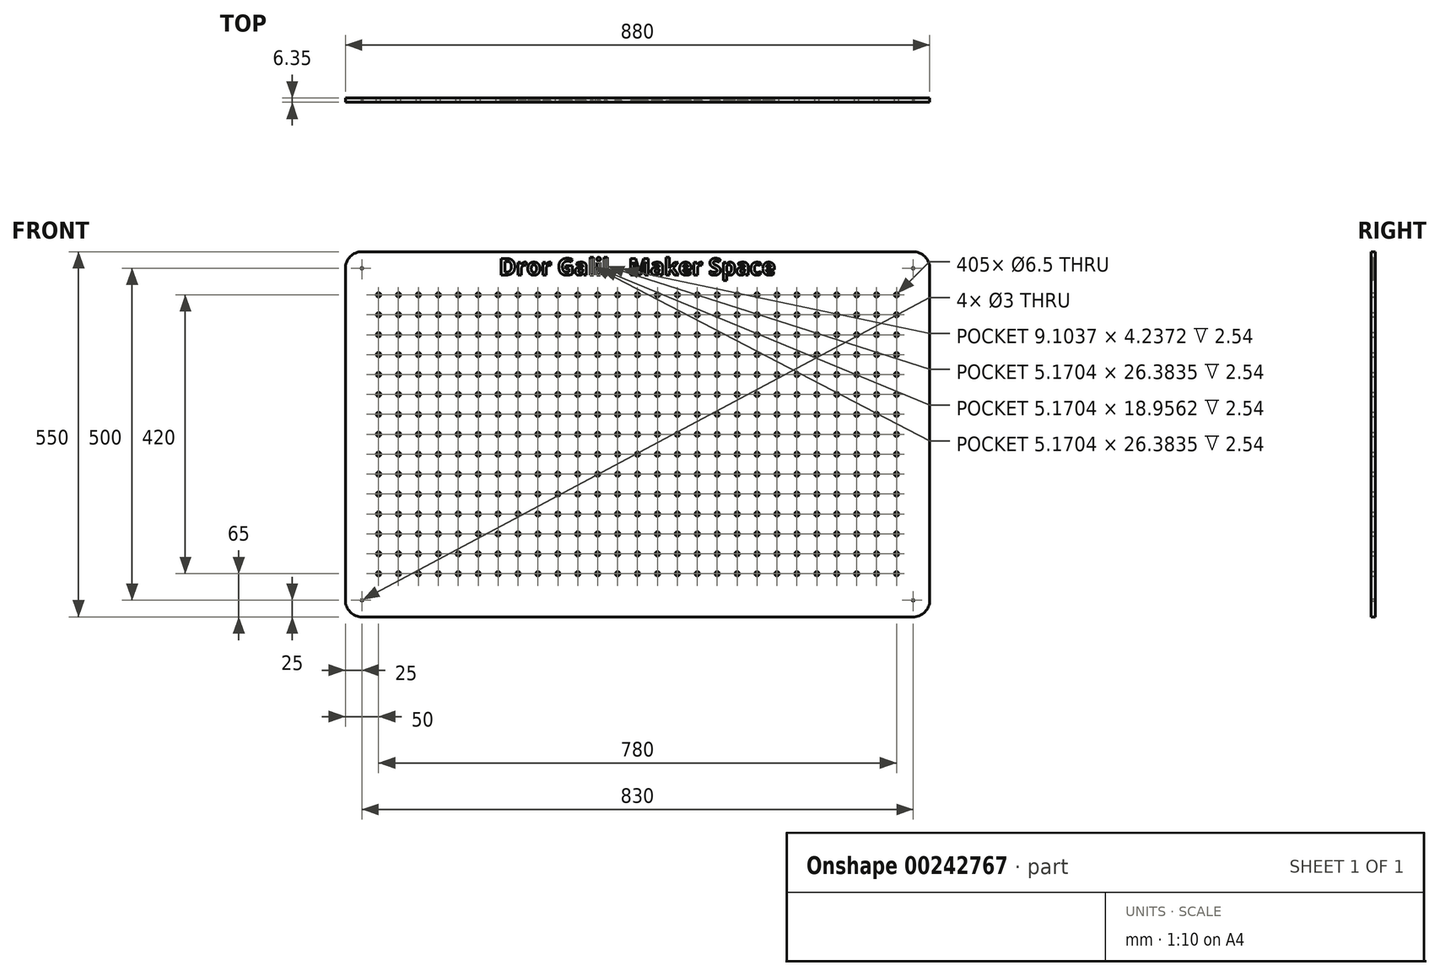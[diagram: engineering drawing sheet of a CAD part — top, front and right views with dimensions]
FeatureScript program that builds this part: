
annotation { "Feature Type Name" : "Feature", "Feature Type Description" : "" }
export const myFeature = defineFeature(function(context is Context, id is Id, definition is map)
    precondition{}
    {
        {
            var Q0;
            Q0=qCreatedBy(makeId("Front.planeOp"),FACE);
            var sketch = newSketch(context, id + "F0", { "sketchPlane" : qUnion([Q0])});
            skLineSegment(sketch, "E0.bottom", {"start": v(-440, 275) * mm, "end": v(440, 275) * mm});
            skLineSegment(sketch, "E0.top", {"start": v(-440, -275) * mm, "end": v(440, -275) * mm});
            skLineSegment(sketch, "E0.left", {"start": v(-440, 275) * mm, "end": v(-440, -275) * mm});
            skLineSegment(sketch, "E1", {"start": v(-390, 275) * mm, "end": v(-390, 210) * mm, "construction": true});
            skLineSegment(sketch, "E2", {"start": v(-390, 210) * mm, "end": v(-440, 210) * mm, "construction": true});
            skCircle(sketch, "E3", {"center": v(-390, 210) * mm, "radius": 3.25 * mm});
            skLineSegment(sketch, "E4", {"start": v(440, 275) * mm, "end": v(440, -275) * mm});
            skLineSegment(sketch, "E5", {"start": v(-48.1, 0) * mm, "end": v(43.52, 0) * mm, "construction": true});
            skLineSegment(sketch, "E6", {"start": v(0, 55.66) * mm, "end": v(0, -47.1) * mm, "construction": true});
            skCircle(sketch, "E7.0.1.0", {"center": v(-390, 180) * mm, "radius": 3.25 * mm});
            skCircle(sketch, "E7.0.2.0", {"center": v(-390, 150) * mm, "radius": 3.25 * mm});
            skCircle(sketch, "E7.0.3.0", {"center": v(-390, 120) * mm, "radius": 3.25 * mm});
            skCircle(sketch, "E7.0.4.0", {"center": v(-390, 90) * mm, "radius": 3.25 * mm});
            skCircle(sketch, "E7.0.5.0", {"center": v(-390, 60) * mm, "radius": 3.25 * mm});
            skCircle(sketch, "E7.0.6.0", {"center": v(-390, 30) * mm, "radius": 3.25 * mm});
            skCircle(sketch, "E7.0.7.0", {"center": v(-390, 0) * mm, "radius": 3.25 * mm});
            skCircle(sketch, "E7.0.8.0", {"center": v(-390, -30) * mm, "radius": 3.25 * mm});
            skCircle(sketch, "E7.1.0.0", {"center": v(-360, 210) * mm, "radius": 3.25 * mm});
            skCircle(sketch, "E7.1.1.0", {"center": v(-360, 180) * mm, "radius": 3.25 * mm});
            skCircle(sketch, "E7.1.2.0", {"center": v(-360, 150) * mm, "radius": 3.25 * mm});
            skCircle(sketch, "E7.1.3.0", {"center": v(-360, 120) * mm, "radius": 3.25 * mm});
            skCircle(sketch, "E7.1.4.0", {"center": v(-360, 90) * mm, "radius": 3.25 * mm});
            skCircle(sketch, "E7.1.5.0", {"center": v(-360, 60) * mm, "radius": 3.25 * mm});
            skCircle(sketch, "E7.1.6.0", {"center": v(-360, 30) * mm, "radius": 3.25 * mm});
            skCircle(sketch, "E7.1.7.0", {"center": v(-360, 0) * mm, "radius": 3.25 * mm});
            skCircle(sketch, "E7.1.8.0", {"center": v(-360, -30) * mm, "radius": 3.25 * mm});
            skCircle(sketch, "E7.2.0.0", {"center": v(-330, 210) * mm, "radius": 3.25 * mm});
            skCircle(sketch, "E7.2.1.0", {"center": v(-330, 180) * mm, "radius": 3.25 * mm});
            skCircle(sketch, "E7.2.2.0", {"center": v(-330, 150) * mm, "radius": 3.25 * mm});
            skCircle(sketch, "E7.2.3.0", {"center": v(-330, 120) * mm, "radius": 3.25 * mm});
            skCircle(sketch, "E7.2.4.0", {"center": v(-330, 90) * mm, "radius": 3.25 * mm});
            skCircle(sketch, "E7.2.5.0", {"center": v(-330, 60) * mm, "radius": 3.25 * mm});
            skCircle(sketch, "E7.2.6.0", {"center": v(-330, 30) * mm, "radius": 3.25 * mm});
            skCircle(sketch, "E7.2.7.0", {"center": v(-330, 0) * mm, "radius": 3.25 * mm});
            skCircle(sketch, "E7.2.8.0", {"center": v(-330, -30) * mm, "radius": 3.25 * mm});
            skCircle(sketch, "E7.3.0.0", {"center": v(-300, 210) * mm, "radius": 3.25 * mm});
            skCircle(sketch, "E7.3.1.0", {"center": v(-300, 180) * mm, "radius": 3.25 * mm});
            skCircle(sketch, "E7.3.2.0", {"center": v(-300, 150) * mm, "radius": 3.25 * mm});
            skCircle(sketch, "E7.3.3.0", {"center": v(-300, 120) * mm, "radius": 3.25 * mm});
            skCircle(sketch, "E7.3.4.0", {"center": v(-300, 90) * mm, "radius": 3.25 * mm});
            skCircle(sketch, "E7.3.5.0", {"center": v(-300, 60) * mm, "radius": 3.25 * mm});
            skCircle(sketch, "E7.3.6.0", {"center": v(-300, 30) * mm, "radius": 3.25 * mm});
            skCircle(sketch, "E7.3.7.0", {"center": v(-300, 0) * mm, "radius": 3.25 * mm});
            skCircle(sketch, "E7.3.8.0", {"center": v(-300, -30) * mm, "radius": 3.25 * mm});
            skCircle(sketch, "E7.4.0.0", {"center": v(-270, 210) * mm, "radius": 3.25 * mm});
            skCircle(sketch, "E7.4.1.0", {"center": v(-270, 180) * mm, "radius": 3.25 * mm});
            skCircle(sketch, "E7.4.2.0", {"center": v(-270, 150) * mm, "radius": 3.25 * mm});
            skCircle(sketch, "E7.4.3.0", {"center": v(-270, 120) * mm, "radius": 3.25 * mm});
            skCircle(sketch, "E7.4.4.0", {"center": v(-270, 90) * mm, "radius": 3.25 * mm});
            skCircle(sketch, "E7.4.5.0", {"center": v(-270, 60) * mm, "radius": 3.25 * mm});
            skCircle(sketch, "E7.4.6.0", {"center": v(-270, 30) * mm, "radius": 3.25 * mm});
            skCircle(sketch, "E7.4.7.0", {"center": v(-270, 0) * mm, "radius": 3.25 * mm});
            skCircle(sketch, "E7.4.8.0", {"center": v(-270, -30) * mm, "radius": 3.25 * mm});
            skCircle(sketch, "E7.5.0.0", {"center": v(-240, 210) * mm, "radius": 3.25 * mm});
            skCircle(sketch, "E7.5.1.0", {"center": v(-240, 180) * mm, "radius": 3.25 * mm});
            skCircle(sketch, "E7.5.2.0", {"center": v(-240, 150) * mm, "radius": 3.25 * mm});
            skCircle(sketch, "E7.5.3.0", {"center": v(-240, 120) * mm, "radius": 3.25 * mm});
            skCircle(sketch, "E7.5.4.0", {"center": v(-240, 90) * mm, "radius": 3.25 * mm});
            skCircle(sketch, "E7.5.5.0", {"center": v(-240, 60) * mm, "radius": 3.25 * mm});
            skCircle(sketch, "E7.5.6.0", {"center": v(-240, 30) * mm, "radius": 3.25 * mm});
            skCircle(sketch, "E7.5.7.0", {"center": v(-240, 0) * mm, "radius": 3.25 * mm});
            skCircle(sketch, "E7.5.8.0", {"center": v(-240, -30) * mm, "radius": 3.25 * mm});
            skCircle(sketch, "E7.6.0.0", {"center": v(-210, 210) * mm, "radius": 3.25 * mm});
            skCircle(sketch, "E7.6.1.0", {"center": v(-210, 180) * mm, "radius": 3.25 * mm});
            skCircle(sketch, "E7.6.2.0", {"center": v(-210, 150) * mm, "radius": 3.25 * mm});
            skCircle(sketch, "E7.6.3.0", {"center": v(-210, 120) * mm, "radius": 3.25 * mm});
            skCircle(sketch, "E7.6.4.0", {"center": v(-210, 90) * mm, "radius": 3.25 * mm});
            skCircle(sketch, "E7.6.5.0", {"center": v(-210, 60) * mm, "radius": 3.25 * mm});
            skCircle(sketch, "E7.6.6.0", {"center": v(-210, 30) * mm, "radius": 3.25 * mm});
            skCircle(sketch, "E7.6.7.0", {"center": v(-210, 0) * mm, "radius": 3.25 * mm});
            skCircle(sketch, "E7.6.8.0", {"center": v(-210, -30) * mm, "radius": 3.25 * mm});
            skCircle(sketch, "E7.7.0.0", {"center": v(-180, 210) * mm, "radius": 3.25 * mm});
            skCircle(sketch, "E7.7.1.0", {"center": v(-180, 180) * mm, "radius": 3.25 * mm});
            skCircle(sketch, "E7.7.2.0", {"center": v(-180, 150) * mm, "radius": 3.25 * mm});
            skCircle(sketch, "E7.7.3.0", {"center": v(-180, 120) * mm, "radius": 3.25 * mm});
            skCircle(sketch, "E7.7.4.0", {"center": v(-180, 90) * mm, "radius": 3.25 * mm});
            skCircle(sketch, "E7.7.5.0", {"center": v(-180, 60) * mm, "radius": 3.25 * mm});
            skCircle(sketch, "E7.7.6.0", {"center": v(-180, 30) * mm, "radius": 3.25 * mm});
            skCircle(sketch, "E7.7.7.0", {"center": v(-180, 0) * mm, "radius": 3.25 * mm});
            skCircle(sketch, "E7.7.8.0", {"center": v(-180, -30) * mm, "radius": 3.25 * mm});
            skCircle(sketch, "E7.8.0.0", {"center": v(-150, 210) * mm, "radius": 3.25 * mm});
            skCircle(sketch, "E7.8.1.0", {"center": v(-150, 180) * mm, "radius": 3.25 * mm});
            skCircle(sketch, "E7.8.2.0", {"center": v(-150, 150) * mm, "radius": 3.25 * mm});
            skCircle(sketch, "E7.8.3.0", {"center": v(-150, 120) * mm, "radius": 3.25 * mm});
            skCircle(sketch, "E7.8.4.0", {"center": v(-150, 90) * mm, "radius": 3.25 * mm});
            skCircle(sketch, "E7.8.5.0", {"center": v(-150, 60) * mm, "radius": 3.25 * mm});
            skCircle(sketch, "E7.8.6.0", {"center": v(-150, 30) * mm, "radius": 3.25 * mm});
            skCircle(sketch, "E7.8.7.0", {"center": v(-150, 0) * mm, "radius": 3.25 * mm});
            skCircle(sketch, "E7.8.8.0", {"center": v(-150, -30) * mm, "radius": 3.25 * mm});
            skCircle(sketch, "E7.9.0.0", {"center": v(-120, 210) * mm, "radius": 3.25 * mm});
            skCircle(sketch, "E7.9.1.0", {"center": v(-120, 180) * mm, "radius": 3.25 * mm});
            skCircle(sketch, "E7.9.2.0", {"center": v(-120, 150) * mm, "radius": 3.25 * mm});
            skCircle(sketch, "E7.9.3.0", {"center": v(-120, 120) * mm, "radius": 3.25 * mm});
            skCircle(sketch, "E7.9.4.0", {"center": v(-120, 90) * mm, "radius": 3.25 * mm});
            skCircle(sketch, "E7.9.5.0", {"center": v(-120, 60) * mm, "radius": 3.25 * mm});
            skCircle(sketch, "E7.9.6.0", {"center": v(-120, 30) * mm, "radius": 3.25 * mm});
            skCircle(sketch, "E7.9.7.0", {"center": v(-120, 0) * mm, "radius": 3.25 * mm});
            skCircle(sketch, "E7.9.8.0", {"center": v(-120, -30) * mm, "radius": 3.25 * mm});
            skCircle(sketch, "E7.10.0.0", {"center": v(-90, 210) * mm, "radius": 3.25 * mm});
            skCircle(sketch, "E7.10.1.0", {"center": v(-90, 180) * mm, "radius": 3.25 * mm});
            skCircle(sketch, "E7.10.2.0", {"center": v(-90, 150) * mm, "radius": 3.25 * mm});
            skCircle(sketch, "E7.10.3.0", {"center": v(-90, 120) * mm, "radius": 3.25 * mm});
            skCircle(sketch, "E7.10.4.0", {"center": v(-90, 90) * mm, "radius": 3.25 * mm});
            skCircle(sketch, "E7.10.5.0", {"center": v(-90, 60) * mm, "radius": 3.25 * mm});
            skCircle(sketch, "E7.10.6.0", {"center": v(-90, 30) * mm, "radius": 3.25 * mm});
            skCircle(sketch, "E7.10.7.0", {"center": v(-90, 0) * mm, "radius": 3.25 * mm});
            skCircle(sketch, "E7.10.8.0", {"center": v(-90, -30) * mm, "radius": 3.25 * mm});
            skCircle(sketch, "E7.11.0.0", {"center": v(-60, 210) * mm, "radius": 3.25 * mm});
            skCircle(sketch, "E7.11.1.0", {"center": v(-60, 180) * mm, "radius": 3.25 * mm});
            skCircle(sketch, "E7.11.2.0", {"center": v(-60, 150) * mm, "radius": 3.25 * mm});
            skCircle(sketch, "E7.11.3.0", {"center": v(-60, 120) * mm, "radius": 3.25 * mm});
            skCircle(sketch, "E7.11.4.0", {"center": v(-60, 90) * mm, "radius": 3.25 * mm});
            skCircle(sketch, "E7.11.5.0", {"center": v(-60, 60) * mm, "radius": 3.25 * mm});
            skCircle(sketch, "E7.11.6.0", {"center": v(-60, 30) * mm, "radius": 3.25 * mm});
            skCircle(sketch, "E7.11.7.0", {"center": v(-60, 0) * mm, "radius": 3.25 * mm});
            skCircle(sketch, "E7.11.8.0", {"center": v(-60, -30) * mm, "radius": 3.25 * mm});
            skCircle(sketch, "E7.12.0.0", {"center": v(-30, 210) * mm, "radius": 3.25 * mm});
            skCircle(sketch, "E7.12.1.0", {"center": v(-30, 180) * mm, "radius": 3.25 * mm});
            skCircle(sketch, "E7.12.2.0", {"center": v(-30, 150) * mm, "radius": 3.25 * mm});
            skCircle(sketch, "E7.12.3.0", {"center": v(-30, 120) * mm, "radius": 3.25 * mm});
            skCircle(sketch, "E7.12.4.0", {"center": v(-30, 90) * mm, "radius": 3.25 * mm});
            skCircle(sketch, "E7.12.5.0", {"center": v(-30, 60) * mm, "radius": 3.25 * mm});
            skCircle(sketch, "E7.12.6.0", {"center": v(-30, 30) * mm, "radius": 3.25 * mm});
            skCircle(sketch, "E7.12.7.0", {"center": v(-30, 0) * mm, "radius": 3.25 * mm});
            skCircle(sketch, "E7.12.8.0", {"center": v(-30, -30) * mm, "radius": 3.25 * mm});
            skCircle(sketch, "E7.13.0.0", {"center": v(0, 210) * mm, "radius": 3.25 * mm});
            skCircle(sketch, "E7.13.1.0", {"center": v(0, 180) * mm, "radius": 3.25 * mm});
            skCircle(sketch, "E7.13.2.0", {"center": v(0, 150) * mm, "radius": 3.25 * mm});
            skCircle(sketch, "E7.13.3.0", {"center": v(0, 120) * mm, "radius": 3.25 * mm});
            skCircle(sketch, "E7.13.4.0", {"center": v(0, 90) * mm, "radius": 3.25 * mm});
            skCircle(sketch, "E7.13.5.0", {"center": v(0, 60) * mm, "radius": 3.25 * mm});
            skCircle(sketch, "E7.13.6.0", {"center": v(0, 30) * mm, "radius": 3.25 * mm});
            skCircle(sketch, "E7.13.7.0", {"center": v(0, 0) * mm, "radius": 3.25 * mm});
            skCircle(sketch, "E7.13.8.0", {"center": v(0, -30) * mm, "radius": 3.25 * mm});
            skCircle(sketch, "E7.14.0.0", {"center": v(30, 210) * mm, "radius": 3.25 * mm});
            skCircle(sketch, "E7.14.1.0", {"center": v(30, 180) * mm, "radius": 3.25 * mm});
            skCircle(sketch, "E7.14.2.0", {"center": v(30, 150) * mm, "radius": 3.25 * mm});
            skCircle(sketch, "E7.14.3.0", {"center": v(30, 120) * mm, "radius": 3.25 * mm});
            skCircle(sketch, "E7.14.4.0", {"center": v(30, 90) * mm, "radius": 3.25 * mm});
            skCircle(sketch, "E7.14.5.0", {"center": v(30, 60) * mm, "radius": 3.25 * mm});
            skCircle(sketch, "E7.14.6.0", {"center": v(30, 30) * mm, "radius": 3.25 * mm});
            skCircle(sketch, "E7.14.7.0", {"center": v(30, 0) * mm, "radius": 3.25 * mm});
            skCircle(sketch, "E7.14.8.0", {"center": v(30, -30) * mm, "radius": 3.25 * mm});
            skLineSegment(sketch, "E7.direction1", {"start": v(-390, 210) * mm, "end": v(-360, 210) * mm, "construction": true});
            skLineSegment(sketch, "E7.direction2", {"start": v(-390, 210) * mm, "end": v(-390, 180) * mm, "construction": true});
            skCircle(sketch, "E8.0.15.0", {"center": v(60, 210) * mm, "radius": 3.25 * mm});
            skCircle(sketch, "E8.0.15.1", {"center": v(60, 180) * mm, "radius": 3.25 * mm});
            skCircle(sketch, "E8.0.15.2", {"center": v(60, 150) * mm, "radius": 3.25 * mm});
            skCircle(sketch, "E8.0.15.3", {"center": v(60, 120) * mm, "radius": 3.25 * mm});
            skCircle(sketch, "E8.0.15.4", {"center": v(60, 90) * mm, "radius": 3.25 * mm});
            skCircle(sketch, "E8.0.15.5", {"center": v(60, 60) * mm, "radius": 3.25 * mm});
            skCircle(sketch, "E8.0.15.6", {"center": v(60, 30) * mm, "radius": 3.25 * mm});
            skCircle(sketch, "E8.0.15.7", {"center": v(60, 0) * mm, "radius": 3.25 * mm});
            skCircle(sketch, "E8.0.15.8", {"center": v(60, -30) * mm, "radius": 3.25 * mm});
            skCircle(sketch, "E8.0.16.0", {"center": v(90, 210) * mm, "radius": 3.25 * mm});
            skCircle(sketch, "E8.0.16.1", {"center": v(90, 180) * mm, "radius": 3.25 * mm});
            skCircle(sketch, "E8.0.16.2", {"center": v(90, 150) * mm, "radius": 3.25 * mm});
            skCircle(sketch, "E8.0.16.3", {"center": v(90, 120) * mm, "radius": 3.25 * mm});
            skCircle(sketch, "E8.0.16.4", {"center": v(90, 90) * mm, "radius": 3.25 * mm});
            skCircle(sketch, "E8.0.16.5", {"center": v(90, 60) * mm, "radius": 3.25 * mm});
            skCircle(sketch, "E8.0.16.6", {"center": v(90, 30) * mm, "radius": 3.25 * mm});
            skCircle(sketch, "E8.0.16.7", {"center": v(90, 0) * mm, "radius": 3.25 * mm});
            skCircle(sketch, "E8.0.16.8", {"center": v(90, -30) * mm, "radius": 3.25 * mm});
            skCircle(sketch, "E8.0.17.0", {"center": v(120, 210) * mm, "radius": 3.25 * mm});
            skCircle(sketch, "E8.0.17.1", {"center": v(120, 180) * mm, "radius": 3.25 * mm});
            skCircle(sketch, "E8.0.17.2", {"center": v(120, 150) * mm, "radius": 3.25 * mm});
            skCircle(sketch, "E8.0.17.3", {"center": v(120, 120) * mm, "radius": 3.25 * mm});
            skCircle(sketch, "E8.0.17.4", {"center": v(120, 90) * mm, "radius": 3.25 * mm});
            skCircle(sketch, "E8.0.17.5", {"center": v(120, 60) * mm, "radius": 3.25 * mm});
            skCircle(sketch, "E8.0.17.6", {"center": v(120, 30) * mm, "radius": 3.25 * mm});
            skCircle(sketch, "E8.0.17.7", {"center": v(120, 0) * mm, "radius": 3.25 * mm});
            skCircle(sketch, "E8.0.17.8", {"center": v(120, -30) * mm, "radius": 3.25 * mm});
            skCircle(sketch, "E8.0.18.0", {"center": v(150, 210) * mm, "radius": 3.25 * mm});
            skCircle(sketch, "E8.0.18.1", {"center": v(150, 180) * mm, "radius": 3.25 * mm});
            skCircle(sketch, "E8.0.18.2", {"center": v(150, 150) * mm, "radius": 3.25 * mm});
            skCircle(sketch, "E8.0.18.3", {"center": v(150, 120) * mm, "radius": 3.25 * mm});
            skCircle(sketch, "E8.0.18.4", {"center": v(150, 90) * mm, "radius": 3.25 * mm});
            skCircle(sketch, "E8.0.18.5", {"center": v(150, 60) * mm, "radius": 3.25 * mm});
            skCircle(sketch, "E8.0.18.6", {"center": v(150, 30) * mm, "radius": 3.25 * mm});
            skCircle(sketch, "E8.0.18.7", {"center": v(150, 0) * mm, "radius": 3.25 * mm});
            skCircle(sketch, "E8.0.18.8", {"center": v(150, -30) * mm, "radius": 3.25 * mm});
            skCircle(sketch, "E8.0.19.0", {"center": v(180, 210) * mm, "radius": 3.25 * mm});
            skCircle(sketch, "E8.0.19.1", {"center": v(180, 180) * mm, "radius": 3.25 * mm});
            skCircle(sketch, "E8.0.19.2", {"center": v(180, 150) * mm, "radius": 3.25 * mm});
            skCircle(sketch, "E8.0.19.3", {"center": v(180, 120) * mm, "radius": 3.25 * mm});
            skCircle(sketch, "E8.0.19.4", {"center": v(180, 90) * mm, "radius": 3.25 * mm});
            skCircle(sketch, "E8.0.19.5", {"center": v(180, 60) * mm, "radius": 3.25 * mm});
            skCircle(sketch, "E8.0.19.6", {"center": v(180, 30) * mm, "radius": 3.25 * mm});
            skCircle(sketch, "E8.0.19.7", {"center": v(180, 0) * mm, "radius": 3.25 * mm});
            skCircle(sketch, "E8.0.19.8", {"center": v(180, -30) * mm, "radius": 3.25 * mm});
            skCircle(sketch, "E8.0.20.0", {"center": v(210, 210) * mm, "radius": 3.25 * mm});
            skCircle(sketch, "E8.0.20.1", {"center": v(210, 180) * mm, "radius": 3.25 * mm});
            skCircle(sketch, "E8.0.20.2", {"center": v(210, 150) * mm, "radius": 3.25 * mm});
            skCircle(sketch, "E8.0.20.3", {"center": v(210, 120) * mm, "radius": 3.25 * mm});
            skCircle(sketch, "E8.0.20.4", {"center": v(210, 90) * mm, "radius": 3.25 * mm});
            skCircle(sketch, "E8.0.20.5", {"center": v(210, 60) * mm, "radius": 3.25 * mm});
            skCircle(sketch, "E8.0.20.6", {"center": v(210, 30) * mm, "radius": 3.25 * mm});
            skCircle(sketch, "E8.0.20.7", {"center": v(210, 0) * mm, "radius": 3.25 * mm});
            skCircle(sketch, "E8.0.20.8", {"center": v(210, -30) * mm, "radius": 3.25 * mm});
            skCircle(sketch, "E8.0.21.0", {"center": v(240, 210) * mm, "radius": 3.25 * mm});
            skCircle(sketch, "E8.0.21.1", {"center": v(240, 180) * mm, "radius": 3.25 * mm});
            skCircle(sketch, "E8.0.21.2", {"center": v(240, 150) * mm, "radius": 3.25 * mm});
            skCircle(sketch, "E8.0.21.3", {"center": v(240, 120) * mm, "radius": 3.25 * mm});
            skCircle(sketch, "E8.0.21.4", {"center": v(240, 90) * mm, "radius": 3.25 * mm});
            skCircle(sketch, "E8.0.21.5", {"center": v(240, 60) * mm, "radius": 3.25 * mm});
            skCircle(sketch, "E8.0.21.6", {"center": v(240, 30) * mm, "radius": 3.25 * mm});
            skCircle(sketch, "E8.0.21.7", {"center": v(240, 0) * mm, "radius": 3.25 * mm});
            skCircle(sketch, "E8.0.21.8", {"center": v(240, -30) * mm, "radius": 3.25 * mm});
            skCircle(sketch, "E8.0.22.0", {"center": v(270, 210) * mm, "radius": 3.25 * mm});
            skCircle(sketch, "E8.0.22.1", {"center": v(270, 180) * mm, "radius": 3.25 * mm});
            skCircle(sketch, "E8.0.22.2", {"center": v(270, 150) * mm, "radius": 3.25 * mm});
            skCircle(sketch, "E8.0.22.3", {"center": v(270, 120) * mm, "radius": 3.25 * mm});
            skCircle(sketch, "E8.0.22.4", {"center": v(270, 90) * mm, "radius": 3.25 * mm});
            skCircle(sketch, "E8.0.22.5", {"center": v(270, 60) * mm, "radius": 3.25 * mm});
            skCircle(sketch, "E8.0.22.6", {"center": v(270, 30) * mm, "radius": 3.25 * mm});
            skCircle(sketch, "E8.0.22.7", {"center": v(270, 0) * mm, "radius": 3.25 * mm});
            skCircle(sketch, "E8.0.22.8", {"center": v(270, -30) * mm, "radius": 3.25 * mm});
            skCircle(sketch, "E8.0.23.0", {"center": v(300, 210) * mm, "radius": 3.25 * mm});
            skCircle(sketch, "E8.0.23.1", {"center": v(300, 180) * mm, "radius": 3.25 * mm});
            skCircle(sketch, "E8.0.23.2", {"center": v(300, 150) * mm, "radius": 3.25 * mm});
            skCircle(sketch, "E8.0.23.3", {"center": v(300, 120) * mm, "radius": 3.25 * mm});
            skCircle(sketch, "E8.0.23.4", {"center": v(300, 90) * mm, "radius": 3.25 * mm});
            skCircle(sketch, "E8.0.23.5", {"center": v(300, 60) * mm, "radius": 3.25 * mm});
            skCircle(sketch, "E8.0.23.6", {"center": v(300, 30) * mm, "radius": 3.25 * mm});
            skCircle(sketch, "E8.0.23.7", {"center": v(300, 0) * mm, "radius": 3.25 * mm});
            skCircle(sketch, "E8.0.23.8", {"center": v(300, -30) * mm, "radius": 3.25 * mm});
            skCircle(sketch, "E8.0.24.0", {"center": v(330, 210) * mm, "radius": 3.25 * mm});
            skCircle(sketch, "E8.0.24.1", {"center": v(330, 180) * mm, "radius": 3.25 * mm});
            skCircle(sketch, "E8.0.24.2", {"center": v(330, 150) * mm, "radius": 3.25 * mm});
            skCircle(sketch, "E8.0.24.3", {"center": v(330, 120) * mm, "radius": 3.25 * mm});
            skCircle(sketch, "E8.0.24.4", {"center": v(330, 90) * mm, "radius": 3.25 * mm});
            skCircle(sketch, "E8.0.24.5", {"center": v(330, 60) * mm, "radius": 3.25 * mm});
            skCircle(sketch, "E8.0.24.6", {"center": v(330, 30) * mm, "radius": 3.25 * mm});
            skCircle(sketch, "E8.0.24.7", {"center": v(330, 0) * mm, "radius": 3.25 * mm});
            skCircle(sketch, "E8.0.24.8", {"center": v(330, -30) * mm, "radius": 3.25 * mm});
            skCircle(sketch, "E9.0.25.0", {"center": v(360, 210) * mm, "radius": 3.25 * mm});
            skCircle(sketch, "E9.0.25.1", {"center": v(360, 180) * mm, "radius": 3.25 * mm});
            skCircle(sketch, "E9.0.25.2", {"center": v(360, 150) * mm, "radius": 3.25 * mm});
            skCircle(sketch, "E9.0.25.3", {"center": v(360, 120) * mm, "radius": 3.25 * mm});
            skCircle(sketch, "E9.0.25.4", {"center": v(360, 90) * mm, "radius": 3.25 * mm});
            skCircle(sketch, "E9.0.25.5", {"center": v(360, 60) * mm, "radius": 3.25 * mm});
            skCircle(sketch, "E9.0.25.6", {"center": v(360, 30) * mm, "radius": 3.25 * mm});
            skCircle(sketch, "E9.0.25.7", {"center": v(360, 0) * mm, "radius": 3.25 * mm});
            skCircle(sketch, "E9.0.25.8", {"center": v(360, -30) * mm, "radius": 3.25 * mm});
            skCircle(sketch, "E9.0.26.0", {"center": v(390, 210) * mm, "radius": 3.25 * mm});
            skCircle(sketch, "E9.0.26.1", {"center": v(390, 180) * mm, "radius": 3.25 * mm});
            skCircle(sketch, "E9.0.26.2", {"center": v(390, 150) * mm, "radius": 3.25 * mm});
            skCircle(sketch, "E9.0.26.3", {"center": v(390, 120) * mm, "radius": 3.25 * mm});
            skCircle(sketch, "E9.0.26.4", {"center": v(390, 90) * mm, "radius": 3.25 * mm});
            skCircle(sketch, "E9.0.26.5", {"center": v(390, 60) * mm, "radius": 3.25 * mm});
            skCircle(sketch, "E9.0.26.6", {"center": v(390, 30) * mm, "radius": 3.25 * mm});
            skCircle(sketch, "E9.0.26.7", {"center": v(390, 0) * mm, "radius": 3.25 * mm});
            skCircle(sketch, "E9.0.26.8", {"center": v(390, -30) * mm, "radius": 3.25 * mm});
            skCircle(sketch, "E10.0.0.9", {"center": v(-390, -60) * mm, "radius": 3.25 * mm});
            skCircle(sketch, "E10.0.0.10", {"center": v(-390, -90) * mm, "radius": 3.25 * mm});
            skCircle(sketch, "E10.0.0.11", {"center": v(-390, -120) * mm, "radius": 3.25 * mm});
            skCircle(sketch, "E10.0.0.12", {"center": v(-390, -150) * mm, "radius": 3.25 * mm});
            skCircle(sketch, "E10.0.0.13", {"center": v(-390, -180) * mm, "radius": 3.25 * mm});
            skCircle(sketch, "E10.0.1.9", {"center": v(-360, -60) * mm, "radius": 3.25 * mm});
            skCircle(sketch, "E10.0.1.10", {"center": v(-360, -90) * mm, "radius": 3.25 * mm});
            skCircle(sketch, "E10.0.1.11", {"center": v(-360, -120) * mm, "radius": 3.25 * mm});
            skCircle(sketch, "E10.0.1.12", {"center": v(-360, -150) * mm, "radius": 3.25 * mm});
            skCircle(sketch, "E10.0.1.13", {"center": v(-360, -180) * mm, "radius": 3.25 * mm});
            skCircle(sketch, "E10.0.2.9", {"center": v(-330, -60) * mm, "radius": 3.25 * mm});
            skCircle(sketch, "E10.0.2.10", {"center": v(-330, -90) * mm, "radius": 3.25 * mm});
            skCircle(sketch, "E10.0.2.11", {"center": v(-330, -120) * mm, "radius": 3.25 * mm});
            skCircle(sketch, "E10.0.2.12", {"center": v(-330, -150) * mm, "radius": 3.25 * mm});
            skCircle(sketch, "E10.0.2.13", {"center": v(-330, -180) * mm, "radius": 3.25 * mm});
            skCircle(sketch, "E10.0.3.9", {"center": v(-300, -60) * mm, "radius": 3.25 * mm});
            skCircle(sketch, "E10.0.3.10", {"center": v(-300, -90) * mm, "radius": 3.25 * mm});
            skCircle(sketch, "E10.0.3.11", {"center": v(-300, -120) * mm, "radius": 3.25 * mm});
            skCircle(sketch, "E10.0.3.12", {"center": v(-300, -150) * mm, "radius": 3.25 * mm});
            skCircle(sketch, "E10.0.3.13", {"center": v(-300, -180) * mm, "radius": 3.25 * mm});
            skCircle(sketch, "E10.0.4.9", {"center": v(-270, -60) * mm, "radius": 3.25 * mm});
            skCircle(sketch, "E10.0.4.10", {"center": v(-270, -90) * mm, "radius": 3.25 * mm});
            skCircle(sketch, "E10.0.4.11", {"center": v(-270, -120) * mm, "radius": 3.25 * mm});
            skCircle(sketch, "E10.0.4.12", {"center": v(-270, -150) * mm, "radius": 3.25 * mm});
            skCircle(sketch, "E10.0.4.13", {"center": v(-270, -180) * mm, "radius": 3.25 * mm});
            skCircle(sketch, "E10.0.5.9", {"center": v(-240, -60) * mm, "radius": 3.25 * mm});
            skCircle(sketch, "E10.0.5.10", {"center": v(-240, -90) * mm, "radius": 3.25 * mm});
            skCircle(sketch, "E10.0.5.11", {"center": v(-240, -120) * mm, "radius": 3.25 * mm});
            skCircle(sketch, "E10.0.5.12", {"center": v(-240, -150) * mm, "radius": 3.25 * mm});
            skCircle(sketch, "E10.0.5.13", {"center": v(-240, -180) * mm, "radius": 3.25 * mm});
            skCircle(sketch, "E10.0.6.9", {"center": v(-210, -60) * mm, "radius": 3.25 * mm});
            skCircle(sketch, "E10.0.6.10", {"center": v(-210, -90) * mm, "radius": 3.25 * mm});
            skCircle(sketch, "E10.0.6.11", {"center": v(-210, -120) * mm, "radius": 3.25 * mm});
            skCircle(sketch, "E10.0.6.12", {"center": v(-210, -150) * mm, "radius": 3.25 * mm});
            skCircle(sketch, "E10.0.6.13", {"center": v(-210, -180) * mm, "radius": 3.25 * mm});
            skCircle(sketch, "E10.0.7.9", {"center": v(-180, -60) * mm, "radius": 3.25 * mm});
            skCircle(sketch, "E10.0.7.10", {"center": v(-180, -90) * mm, "radius": 3.25 * mm});
            skCircle(sketch, "E10.0.7.11", {"center": v(-180, -120) * mm, "radius": 3.25 * mm});
            skCircle(sketch, "E10.0.7.12", {"center": v(-180, -150) * mm, "radius": 3.25 * mm});
            skCircle(sketch, "E10.0.7.13", {"center": v(-180, -180) * mm, "radius": 3.25 * mm});
            skCircle(sketch, "E10.0.8.9", {"center": v(-150, -60) * mm, "radius": 3.25 * mm});
            skCircle(sketch, "E10.0.8.10", {"center": v(-150, -90) * mm, "radius": 3.25 * mm});
            skCircle(sketch, "E10.0.8.11", {"center": v(-150, -120) * mm, "radius": 3.25 * mm});
            skCircle(sketch, "E10.0.8.12", {"center": v(-150, -150) * mm, "radius": 3.25 * mm});
            skCircle(sketch, "E10.0.8.13", {"center": v(-150, -180) * mm, "radius": 3.25 * mm});
            skCircle(sketch, "E10.0.9.9", {"center": v(-120, -60) * mm, "radius": 3.25 * mm});
            skCircle(sketch, "E10.0.9.10", {"center": v(-120, -90) * mm, "radius": 3.25 * mm});
            skCircle(sketch, "E10.0.9.11", {"center": v(-120, -120) * mm, "radius": 3.25 * mm});
            skCircle(sketch, "E10.0.9.12", {"center": v(-120, -150) * mm, "radius": 3.25 * mm});
            skCircle(sketch, "E10.0.9.13", {"center": v(-120, -180) * mm, "radius": 3.25 * mm});
            skCircle(sketch, "E10.0.10.9", {"center": v(-90, -60) * mm, "radius": 3.25 * mm});
            skCircle(sketch, "E10.0.10.10", {"center": v(-90, -90) * mm, "radius": 3.25 * mm});
            skCircle(sketch, "E10.0.10.11", {"center": v(-90, -120) * mm, "radius": 3.25 * mm});
            skCircle(sketch, "E10.0.10.12", {"center": v(-90, -150) * mm, "radius": 3.25 * mm});
            skCircle(sketch, "E10.0.10.13", {"center": v(-90, -180) * mm, "radius": 3.25 * mm});
            skCircle(sketch, "E10.0.11.9", {"center": v(-60, -60) * mm, "radius": 3.25 * mm});
            skCircle(sketch, "E10.0.11.10", {"center": v(-60, -90) * mm, "radius": 3.25 * mm});
            skCircle(sketch, "E10.0.11.11", {"center": v(-60, -120) * mm, "radius": 3.25 * mm});
            skCircle(sketch, "E10.0.11.12", {"center": v(-60, -150) * mm, "radius": 3.25 * mm});
            skCircle(sketch, "E10.0.11.13", {"center": v(-60, -180) * mm, "radius": 3.25 * mm});
            skCircle(sketch, "E10.0.12.9", {"center": v(-30, -60) * mm, "radius": 3.25 * mm});
            skCircle(sketch, "E10.0.12.10", {"center": v(-30, -90) * mm, "radius": 3.25 * mm});
            skCircle(sketch, "E10.0.12.11", {"center": v(-30, -120) * mm, "radius": 3.25 * mm});
            skCircle(sketch, "E10.0.12.12", {"center": v(-30, -150) * mm, "radius": 3.25 * mm});
            skCircle(sketch, "E10.0.12.13", {"center": v(-30, -180) * mm, "radius": 3.25 * mm});
            skCircle(sketch, "E10.0.13.9", {"center": v(0, -60) * mm, "radius": 3.25 * mm});
            skCircle(sketch, "E10.0.13.10", {"center": v(0, -90) * mm, "radius": 3.25 * mm});
            skCircle(sketch, "E10.0.13.11", {"center": v(0, -120) * mm, "radius": 3.25 * mm});
            skCircle(sketch, "E10.0.13.12", {"center": v(0, -150) * mm, "radius": 3.25 * mm});
            skCircle(sketch, "E10.0.13.13", {"center": v(0, -180) * mm, "radius": 3.25 * mm});
            skCircle(sketch, "E10.0.14.9", {"center": v(30, -60) * mm, "radius": 3.25 * mm});
            skCircle(sketch, "E10.0.14.10", {"center": v(30, -90) * mm, "radius": 3.25 * mm});
            skCircle(sketch, "E10.0.14.11", {"center": v(30, -120) * mm, "radius": 3.25 * mm});
            skCircle(sketch, "E10.0.14.12", {"center": v(30, -150) * mm, "radius": 3.25 * mm});
            skCircle(sketch, "E10.0.14.13", {"center": v(30, -180) * mm, "radius": 3.25 * mm});
            skCircle(sketch, "E10.0.15.9", {"center": v(60, -60) * mm, "radius": 3.25 * mm});
            skCircle(sketch, "E10.0.15.10", {"center": v(60, -90) * mm, "radius": 3.25 * mm});
            skCircle(sketch, "E10.0.15.11", {"center": v(60, -120) * mm, "radius": 3.25 * mm});
            skCircle(sketch, "E10.0.15.12", {"center": v(60, -150) * mm, "radius": 3.25 * mm});
            skCircle(sketch, "E10.0.15.13", {"center": v(60, -180) * mm, "radius": 3.25 * mm});
            skCircle(sketch, "E10.0.16.9", {"center": v(90, -60) * mm, "radius": 3.25 * mm});
            skCircle(sketch, "E10.0.16.10", {"center": v(90, -90) * mm, "radius": 3.25 * mm});
            skCircle(sketch, "E10.0.16.11", {"center": v(90, -120) * mm, "radius": 3.25 * mm});
            skCircle(sketch, "E10.0.16.12", {"center": v(90, -150) * mm, "radius": 3.25 * mm});
            skCircle(sketch, "E10.0.16.13", {"center": v(90, -180) * mm, "radius": 3.25 * mm});
            skCircle(sketch, "E10.0.17.9", {"center": v(120, -60) * mm, "radius": 3.25 * mm});
            skCircle(sketch, "E10.0.17.10", {"center": v(120, -90) * mm, "radius": 3.25 * mm});
            skCircle(sketch, "E10.0.17.11", {"center": v(120, -120) * mm, "radius": 3.25 * mm});
            skCircle(sketch, "E10.0.17.12", {"center": v(120, -150) * mm, "radius": 3.25 * mm});
            skCircle(sketch, "E10.0.17.13", {"center": v(120, -180) * mm, "radius": 3.25 * mm});
            skCircle(sketch, "E10.0.18.9", {"center": v(150, -60) * mm, "radius": 3.25 * mm});
            skCircle(sketch, "E10.0.18.10", {"center": v(150, -90) * mm, "radius": 3.25 * mm});
            skCircle(sketch, "E10.0.18.11", {"center": v(150, -120) * mm, "radius": 3.25 * mm});
            skCircle(sketch, "E10.0.18.12", {"center": v(150, -150) * mm, "radius": 3.25 * mm});
            skCircle(sketch, "E10.0.18.13", {"center": v(150, -180) * mm, "radius": 3.25 * mm});
            skCircle(sketch, "E10.0.19.9", {"center": v(180, -60) * mm, "radius": 3.25 * mm});
            skCircle(sketch, "E10.0.19.10", {"center": v(180, -90) * mm, "radius": 3.25 * mm});
            skCircle(sketch, "E10.0.19.11", {"center": v(180, -120) * mm, "radius": 3.25 * mm});
            skCircle(sketch, "E10.0.19.12", {"center": v(180, -150) * mm, "radius": 3.25 * mm});
            skCircle(sketch, "E10.0.19.13", {"center": v(180, -180) * mm, "radius": 3.25 * mm});
            skCircle(sketch, "E10.0.20.9", {"center": v(210, -60) * mm, "radius": 3.25 * mm});
            skCircle(sketch, "E10.0.20.10", {"center": v(210, -90) * mm, "radius": 3.25 * mm});
            skCircle(sketch, "E10.0.20.11", {"center": v(210, -120) * mm, "radius": 3.25 * mm});
            skCircle(sketch, "E10.0.20.12", {"center": v(210, -150) * mm, "radius": 3.25 * mm});
            skCircle(sketch, "E10.0.20.13", {"center": v(210, -180) * mm, "radius": 3.25 * mm});
            skCircle(sketch, "E10.0.21.9", {"center": v(240, -60) * mm, "radius": 3.25 * mm});
            skCircle(sketch, "E10.0.21.10", {"center": v(240, -90) * mm, "radius": 3.25 * mm});
            skCircle(sketch, "E10.0.21.11", {"center": v(240, -120) * mm, "radius": 3.25 * mm});
            skCircle(sketch, "E10.0.21.12", {"center": v(240, -150) * mm, "radius": 3.25 * mm});
            skCircle(sketch, "E10.0.21.13", {"center": v(240, -180) * mm, "radius": 3.25 * mm});
            skCircle(sketch, "E10.0.22.9", {"center": v(270, -60) * mm, "radius": 3.25 * mm});
            skCircle(sketch, "E10.0.22.10", {"center": v(270, -90) * mm, "radius": 3.25 * mm});
            skCircle(sketch, "E10.0.22.11", {"center": v(270, -120) * mm, "radius": 3.25 * mm});
            skCircle(sketch, "E10.0.22.12", {"center": v(270, -150) * mm, "radius": 3.25 * mm});
            skCircle(sketch, "E10.0.22.13", {"center": v(270, -180) * mm, "radius": 3.25 * mm});
            skCircle(sketch, "E10.0.23.9", {"center": v(300, -60) * mm, "radius": 3.25 * mm});
            skCircle(sketch, "E10.0.23.10", {"center": v(300, -90) * mm, "radius": 3.25 * mm});
            skCircle(sketch, "E10.0.23.11", {"center": v(300, -120) * mm, "radius": 3.25 * mm});
            skCircle(sketch, "E10.0.23.12", {"center": v(300, -150) * mm, "radius": 3.25 * mm});
            skCircle(sketch, "E10.0.23.13", {"center": v(300, -180) * mm, "radius": 3.25 * mm});
            skCircle(sketch, "E10.0.24.9", {"center": v(330, -60) * mm, "radius": 3.25 * mm});
            skCircle(sketch, "E10.0.24.10", {"center": v(330, -90) * mm, "radius": 3.25 * mm});
            skCircle(sketch, "E10.0.24.11", {"center": v(330, -120) * mm, "radius": 3.25 * mm});
            skCircle(sketch, "E10.0.24.12", {"center": v(330, -150) * mm, "radius": 3.25 * mm});
            skCircle(sketch, "E10.0.24.13", {"center": v(330, -180) * mm, "radius": 3.25 * mm});
            skCircle(sketch, "E10.0.25.9", {"center": v(360, -60) * mm, "radius": 3.25 * mm});
            skCircle(sketch, "E10.0.25.10", {"center": v(360, -90) * mm, "radius": 3.25 * mm});
            skCircle(sketch, "E10.0.25.11", {"center": v(360, -120) * mm, "radius": 3.25 * mm});
            skCircle(sketch, "E10.0.25.12", {"center": v(360, -150) * mm, "radius": 3.25 * mm});
            skCircle(sketch, "E10.0.25.13", {"center": v(360, -180) * mm, "radius": 3.25 * mm});
            skCircle(sketch, "E10.0.26.9", {"center": v(390, -60) * mm, "radius": 3.25 * mm});
            skCircle(sketch, "E10.0.26.10", {"center": v(390, -90) * mm, "radius": 3.25 * mm});
            skCircle(sketch, "E10.0.26.11", {"center": v(390, -120) * mm, "radius": 3.25 * mm});
            skCircle(sketch, "E10.0.26.12", {"center": v(390, -150) * mm, "radius": 3.25 * mm});
            skCircle(sketch, "E10.0.26.13", {"center": v(390, -180) * mm, "radius": 3.25 * mm});
            skCircle(sketch, "E11.0.0.14", {"center": v(-390, -210) * mm, "radius": 3.25 * mm});
            skCircle(sketch, "E11.0.1.14", {"center": v(-360, -210) * mm, "radius": 3.25 * mm});
            skCircle(sketch, "E11.0.2.14", {"center": v(-330, -210) * mm, "radius": 3.25 * mm});
            skCircle(sketch, "E11.0.3.14", {"center": v(-300, -210) * mm, "radius": 3.25 * mm});
            skCircle(sketch, "E11.0.4.14", {"center": v(-270, -210) * mm, "radius": 3.25 * mm});
            skCircle(sketch, "E11.0.5.14", {"center": v(-240, -210) * mm, "radius": 3.25 * mm});
            skCircle(sketch, "E11.0.6.14", {"center": v(-210, -210) * mm, "radius": 3.25 * mm});
            skCircle(sketch, "E11.0.7.14", {"center": v(-180, -210) * mm, "radius": 3.25 * mm});
            skCircle(sketch, "E11.0.8.14", {"center": v(-150, -210) * mm, "radius": 3.25 * mm});
            skCircle(sketch, "E11.0.9.14", {"center": v(-120, -210) * mm, "radius": 3.25 * mm});
            skCircle(sketch, "E11.0.10.14", {"center": v(-90, -210) * mm, "radius": 3.25 * mm});
            skCircle(sketch, "E11.0.11.14", {"center": v(-60, -210) * mm, "radius": 3.25 * mm});
            skCircle(sketch, "E11.0.12.14", {"center": v(-30, -210) * mm, "radius": 3.25 * mm});
            skCircle(sketch, "E11.0.13.14", {"center": v(0, -210) * mm, "radius": 3.25 * mm});
            skCircle(sketch, "E11.0.14.14", {"center": v(30, -210) * mm, "radius": 3.25 * mm});
            skCircle(sketch, "E11.0.15.14", {"center": v(60, -210) * mm, "radius": 3.25 * mm});
            skCircle(sketch, "E11.0.16.14", {"center": v(90, -210) * mm, "radius": 3.25 * mm});
            skCircle(sketch, "E11.0.17.14", {"center": v(120, -210) * mm, "radius": 3.25 * mm});
            skCircle(sketch, "E11.0.18.14", {"center": v(150, -210) * mm, "radius": 3.25 * mm});
            skCircle(sketch, "E11.0.19.14", {"center": v(180, -210) * mm, "radius": 3.25 * mm});
            skCircle(sketch, "E11.0.20.14", {"center": v(210, -210) * mm, "radius": 3.25 * mm});
            skCircle(sketch, "E11.0.21.14", {"center": v(240, -210) * mm, "radius": 3.25 * mm});
            skCircle(sketch, "E11.0.22.14", {"center": v(270, -210) * mm, "radius": 3.25 * mm});
            skCircle(sketch, "E11.0.23.14", {"center": v(300, -210) * mm, "radius": 3.25 * mm});
            skCircle(sketch, "E11.0.24.14", {"center": v(330, -210) * mm, "radius": 3.25 * mm});
            skCircle(sketch, "E11.0.25.14", {"center": v(360, -210) * mm, "radius": 3.25 * mm});
            skCircle(sketch, "E11.0.26.14", {"center": v(390, -210) * mm, "radius": 3.25 * mm});
            skSolve(sketch);
        }
        {
            var Q0;
            Q0 = qSketchRegion(id + "F0", true);
            extrude(context, id + "F1", {"entities" : qUnion([Q0]), "depth" : 6.35 * mm});
        }
        {
            var Q0;
            Q0=makeQuery(id+"F1.opExtrude","CAP_FACE",FACE,{"disambiguationData":[OSD([sQuery(id+"F0.wireOp",EDGE,"E0.bottom"),sQuery(id+"F0.wireOp",EDGE,"E0.top"),sQuery(id+"F0.wireOp",EDGE,"E0.left"),sQuery(id+"F0.wireOp",EDGE,"E3"),sQuery(id+"F0.wireOp",EDGE,"E4"),sQuery(id+"F0.wireOp",EDGE,"E7.0.1.0"),sQuery(id+"F0.wireOp",EDGE,"E7.0.2.0"),sQuery(id+"F0.wireOp",EDGE,"E7.0.3.0"),sQuery(id+"F0.wireOp",EDGE,"E7.0.4.0"),sQuery(id+"F0.wireOp",EDGE,"E7.0.5.0"),sQuery(id+"F0.wireOp",EDGE,"E7.0.6.0"),sQuery(id+"F0.wireOp",EDGE,"E7.0.7.0"),sQuery(id+"F0.wireOp",EDGE,"E7.0.8.0"),sQuery(id+"F0.wireOp",EDGE,"E7.1.0.0"),sQuery(id+"F0.wireOp",EDGE,"E7.1.1.0"),sQuery(id+"F0.wireOp",EDGE,"E7.1.2.0"),sQuery(id+"F0.wireOp",EDGE,"E7.1.3.0"),sQuery(id+"F0.wireOp",EDGE,"E7.1.4.0"),sQuery(id+"F0.wireOp",EDGE,"E7.1.5.0"),sQuery(id+"F0.wireOp",EDGE,"E7.1.6.0"),sQuery(id+"F0.wireOp",EDGE,"E7.1.7.0"),sQuery(id+"F0.wireOp",EDGE,"E7.1.8.0"),sQuery(id+"F0.wireOp",EDGE,"E7.2.0.0"),sQuery(id+"F0.wireOp",EDGE,"E7.2.1.0"),sQuery(id+"F0.wireOp",EDGE,"E7.2.2.0"),sQuery(id+"F0.wireOp",EDGE,"E7.2.3.0"),sQuery(id+"F0.wireOp",EDGE,"E7.2.4.0"),sQuery(id+"F0.wireOp",EDGE,"E7.2.5.0"),sQuery(id+"F0.wireOp",EDGE,"E7.2.6.0"),sQuery(id+"F0.wireOp",EDGE,"E7.2.7.0"),sQuery(id+"F0.wireOp",EDGE,"E7.2.8.0"),sQuery(id+"F0.wireOp",EDGE,"E7.3.0.0"),sQuery(id+"F0.wireOp",EDGE,"E7.3.1.0"),sQuery(id+"F0.wireOp",EDGE,"E7.3.2.0"),sQuery(id+"F0.wireOp",EDGE,"E7.3.3.0"),sQuery(id+"F0.wireOp",EDGE,"E7.3.4.0"),sQuery(id+"F0.wireOp",EDGE,"E7.3.5.0"),sQuery(id+"F0.wireOp",EDGE,"E7.3.6.0"),sQuery(id+"F0.wireOp",EDGE,"E7.3.7.0"),sQuery(id+"F0.wireOp",EDGE,"E7.3.8.0"),sQuery(id+"F0.wireOp",EDGE,"E7.4.0.0"),sQuery(id+"F0.wireOp",EDGE,"E7.4.1.0"),sQuery(id+"F0.wireOp",EDGE,"E7.4.2.0"),sQuery(id+"F0.wireOp",EDGE,"E7.4.3.0"),sQuery(id+"F0.wireOp",EDGE,"E7.4.4.0"),sQuery(id+"F0.wireOp",EDGE,"E7.4.5.0"),sQuery(id+"F0.wireOp",EDGE,"E7.4.6.0"),sQuery(id+"F0.wireOp",EDGE,"E7.4.7.0"),sQuery(id+"F0.wireOp",EDGE,"E7.4.8.0"),sQuery(id+"F0.wireOp",EDGE,"E7.5.0.0"),sQuery(id+"F0.wireOp",EDGE,"E7.5.1.0"),sQuery(id+"F0.wireOp",EDGE,"E7.5.2.0"),sQuery(id+"F0.wireOp",EDGE,"E7.5.3.0"),sQuery(id+"F0.wireOp",EDGE,"E7.5.4.0"),sQuery(id+"F0.wireOp",EDGE,"E7.5.5.0"),sQuery(id+"F0.wireOp",EDGE,"E7.5.6.0"),sQuery(id+"F0.wireOp",EDGE,"E7.5.7.0"),sQuery(id+"F0.wireOp",EDGE,"E7.5.8.0"),sQuery(id+"F0.wireOp",EDGE,"E7.6.0.0"),sQuery(id+"F0.wireOp",EDGE,"E7.6.1.0"),sQuery(id+"F0.wireOp",EDGE,"E7.6.2.0"),sQuery(id+"F0.wireOp",EDGE,"E7.6.3.0"),sQuery(id+"F0.wireOp",EDGE,"E7.6.4.0"),sQuery(id+"F0.wireOp",EDGE,"E7.6.5.0"),sQuery(id+"F0.wireOp",EDGE,"E7.6.6.0"),sQuery(id+"F0.wireOp",EDGE,"E7.6.7.0"),sQuery(id+"F0.wireOp",EDGE,"E7.6.8.0"),sQuery(id+"F0.wireOp",EDGE,"E7.7.0.0"),sQuery(id+"F0.wireOp",EDGE,"E7.7.1.0"),sQuery(id+"F0.wireOp",EDGE,"E7.7.2.0"),sQuery(id+"F0.wireOp",EDGE,"E7.7.3.0"),sQuery(id+"F0.wireOp",EDGE,"E7.7.4.0"),sQuery(id+"F0.wireOp",EDGE,"E7.7.5.0"),sQuery(id+"F0.wireOp",EDGE,"E7.7.6.0"),sQuery(id+"F0.wireOp",EDGE,"E7.7.7.0"),sQuery(id+"F0.wireOp",EDGE,"E7.7.8.0"),sQuery(id+"F0.wireOp",EDGE,"E7.8.0.0"),sQuery(id+"F0.wireOp",EDGE,"E7.8.1.0"),sQuery(id+"F0.wireOp",EDGE,"E7.8.2.0"),sQuery(id+"F0.wireOp",EDGE,"E7.8.3.0"),sQuery(id+"F0.wireOp",EDGE,"E7.8.4.0"),sQuery(id+"F0.wireOp",EDGE,"E7.8.5.0"),sQuery(id+"F0.wireOp",EDGE,"E7.8.6.0"),sQuery(id+"F0.wireOp",EDGE,"E7.8.7.0"),sQuery(id+"F0.wireOp",EDGE,"E7.8.8.0"),sQuery(id+"F0.wireOp",EDGE,"E7.9.0.0"),sQuery(id+"F0.wireOp",EDGE,"E7.9.1.0"),sQuery(id+"F0.wireOp",EDGE,"E7.9.2.0"),sQuery(id+"F0.wireOp",EDGE,"E7.9.3.0"),sQuery(id+"F0.wireOp",EDGE,"E7.9.4.0"),sQuery(id+"F0.wireOp",EDGE,"E7.9.5.0"),sQuery(id+"F0.wireOp",EDGE,"E7.9.6.0"),sQuery(id+"F0.wireOp",EDGE,"E7.9.7.0"),sQuery(id+"F0.wireOp",EDGE,"E7.9.8.0"),sQuery(id+"F0.wireOp",EDGE,"E7.10.0.0"),sQuery(id+"F0.wireOp",EDGE,"E7.10.1.0"),sQuery(id+"F0.wireOp",EDGE,"E7.10.2.0"),sQuery(id+"F0.wireOp",EDGE,"E7.10.3.0"),sQuery(id+"F0.wireOp",EDGE,"E7.10.4.0"),sQuery(id+"F0.wireOp",EDGE,"E7.10.5.0"),sQuery(id+"F0.wireOp",EDGE,"E7.10.6.0"),sQuery(id+"F0.wireOp",EDGE,"E7.10.7.0"),sQuery(id+"F0.wireOp",EDGE,"E7.10.8.0"),sQuery(id+"F0.wireOp",EDGE,"E7.11.0.0"),sQuery(id+"F0.wireOp",EDGE,"E7.11.1.0"),sQuery(id+"F0.wireOp",EDGE,"E7.11.2.0"),sQuery(id+"F0.wireOp",EDGE,"E7.11.3.0"),sQuery(id+"F0.wireOp",EDGE,"E7.11.4.0"),sQuery(id+"F0.wireOp",EDGE,"E7.11.5.0"),sQuery(id+"F0.wireOp",EDGE,"E7.11.6.0"),sQuery(id+"F0.wireOp",EDGE,"E7.11.7.0"),sQuery(id+"F0.wireOp",EDGE,"E7.11.8.0"),sQuery(id+"F0.wireOp",EDGE,"E7.12.0.0"),sQuery(id+"F0.wireOp",EDGE,"E7.12.1.0"),sQuery(id+"F0.wireOp",EDGE,"E7.12.2.0"),sQuery(id+"F0.wireOp",EDGE,"E7.12.3.0"),sQuery(id+"F0.wireOp",EDGE,"E7.12.4.0"),sQuery(id+"F0.wireOp",EDGE,"E7.12.5.0"),sQuery(id+"F0.wireOp",EDGE,"E7.12.6.0"),sQuery(id+"F0.wireOp",EDGE,"E7.12.7.0"),sQuery(id+"F0.wireOp",EDGE,"E7.12.8.0"),sQuery(id+"F0.wireOp",EDGE,"E7.13.0.0"),sQuery(id+"F0.wireOp",EDGE,"E7.13.1.0"),sQuery(id+"F0.wireOp",EDGE,"E7.13.2.0"),sQuery(id+"F0.wireOp",EDGE,"E7.13.3.0"),sQuery(id+"F0.wireOp",EDGE,"E7.13.4.0"),sQuery(id+"F0.wireOp",EDGE,"E7.13.5.0"),sQuery(id+"F0.wireOp",EDGE,"E7.13.6.0"),sQuery(id+"F0.wireOp",EDGE,"E7.13.7.0"),sQuery(id+"F0.wireOp",EDGE,"E7.13.8.0"),sQuery(id+"F0.wireOp",EDGE,"E7.14.0.0"),sQuery(id+"F0.wireOp",EDGE,"E7.14.1.0"),sQuery(id+"F0.wireOp",EDGE,"E7.14.2.0"),sQuery(id+"F0.wireOp",EDGE,"E7.14.3.0"),sQuery(id+"F0.wireOp",EDGE,"E7.14.4.0"),sQuery(id+"F0.wireOp",EDGE,"E7.14.5.0"),sQuery(id+"F0.wireOp",EDGE,"E7.14.6.0"),sQuery(id+"F0.wireOp",EDGE,"E7.14.7.0"),sQuery(id+"F0.wireOp",EDGE,"E7.14.8.0"),sQuery(id+"F0.wireOp",EDGE,"E8.0.15.0"),sQuery(id+"F0.wireOp",EDGE,"E8.0.15.1"),sQuery(id+"F0.wireOp",EDGE,"E8.0.15.2"),sQuery(id+"F0.wireOp",EDGE,"E8.0.15.3"),sQuery(id+"F0.wireOp",EDGE,"E8.0.15.4"),sQuery(id+"F0.wireOp",EDGE,"E8.0.15.5"),sQuery(id+"F0.wireOp",EDGE,"E8.0.15.6"),sQuery(id+"F0.wireOp",EDGE,"E8.0.15.7"),sQuery(id+"F0.wireOp",EDGE,"E8.0.15.8"),sQuery(id+"F0.wireOp",EDGE,"E8.0.16.0"),sQuery(id+"F0.wireOp",EDGE,"E8.0.16.1"),sQuery(id+"F0.wireOp",EDGE,"E8.0.16.2"),sQuery(id+"F0.wireOp",EDGE,"E8.0.16.3"),sQuery(id+"F0.wireOp",EDGE,"E8.0.16.4"),sQuery(id+"F0.wireOp",EDGE,"E8.0.16.5"),sQuery(id+"F0.wireOp",EDGE,"E8.0.16.6"),sQuery(id+"F0.wireOp",EDGE,"E8.0.16.7"),sQuery(id+"F0.wireOp",EDGE,"E8.0.16.8"),sQuery(id+"F0.wireOp",EDGE,"E8.0.17.0"),sQuery(id+"F0.wireOp",EDGE,"E8.0.17.1"),sQuery(id+"F0.wireOp",EDGE,"E8.0.17.2"),sQuery(id+"F0.wireOp",EDGE,"E8.0.17.3"),sQuery(id+"F0.wireOp",EDGE,"E8.0.17.4"),sQuery(id+"F0.wireOp",EDGE,"E8.0.17.5"),sQuery(id+"F0.wireOp",EDGE,"E8.0.17.6"),sQuery(id+"F0.wireOp",EDGE,"E8.0.17.7"),sQuery(id+"F0.wireOp",EDGE,"E8.0.17.8"),sQuery(id+"F0.wireOp",EDGE,"E8.0.18.0"),sQuery(id+"F0.wireOp",EDGE,"E8.0.18.1"),sQuery(id+"F0.wireOp",EDGE,"E8.0.18.2"),sQuery(id+"F0.wireOp",EDGE,"E8.0.18.3"),sQuery(id+"F0.wireOp",EDGE,"E8.0.18.4"),sQuery(id+"F0.wireOp",EDGE,"E8.0.18.5"),sQuery(id+"F0.wireOp",EDGE,"E8.0.18.6"),sQuery(id+"F0.wireOp",EDGE,"E8.0.18.7"),sQuery(id+"F0.wireOp",EDGE,"E8.0.18.8"),sQuery(id+"F0.wireOp",EDGE,"E8.0.19.0"),sQuery(id+"F0.wireOp",EDGE,"E8.0.19.1"),sQuery(id+"F0.wireOp",EDGE,"E8.0.19.2"),sQuery(id+"F0.wireOp",EDGE,"E8.0.19.3"),sQuery(id+"F0.wireOp",EDGE,"E8.0.19.4"),sQuery(id+"F0.wireOp",EDGE,"E8.0.19.5"),sQuery(id+"F0.wireOp",EDGE,"E8.0.19.6"),sQuery(id+"F0.wireOp",EDGE,"E8.0.19.7"),sQuery(id+"F0.wireOp",EDGE,"E8.0.19.8"),sQuery(id+"F0.wireOp",EDGE,"E8.0.20.0"),sQuery(id+"F0.wireOp",EDGE,"E8.0.20.1"),sQuery(id+"F0.wireOp",EDGE,"E8.0.20.2"),sQuery(id+"F0.wireOp",EDGE,"E8.0.20.3"),sQuery(id+"F0.wireOp",EDGE,"E8.0.20.4"),sQuery(id+"F0.wireOp",EDGE,"E8.0.20.5"),sQuery(id+"F0.wireOp",EDGE,"E8.0.20.6"),sQuery(id+"F0.wireOp",EDGE,"E8.0.20.7"),sQuery(id+"F0.wireOp",EDGE,"E8.0.20.8"),sQuery(id+"F0.wireOp",EDGE,"E8.0.21.0"),sQuery(id+"F0.wireOp",EDGE,"E8.0.21.1"),sQuery(id+"F0.wireOp",EDGE,"E8.0.21.2"),sQuery(id+"F0.wireOp",EDGE,"E8.0.21.3"),sQuery(id+"F0.wireOp",EDGE,"E8.0.21.4"),sQuery(id+"F0.wireOp",EDGE,"E8.0.21.5"),sQuery(id+"F0.wireOp",EDGE,"E8.0.21.6"),sQuery(id+"F0.wireOp",EDGE,"E8.0.21.7"),sQuery(id+"F0.wireOp",EDGE,"E8.0.21.8"),sQuery(id+"F0.wireOp",EDGE,"E8.0.22.0"),sQuery(id+"F0.wireOp",EDGE,"E8.0.22.1"),sQuery(id+"F0.wireOp",EDGE,"E8.0.22.2"),sQuery(id+"F0.wireOp",EDGE,"E8.0.22.3"),sQuery(id+"F0.wireOp",EDGE,"E8.0.22.4"),sQuery(id+"F0.wireOp",EDGE,"E8.0.22.5"),sQuery(id+"F0.wireOp",EDGE,"E8.0.22.6"),sQuery(id+"F0.wireOp",EDGE,"E8.0.22.7"),sQuery(id+"F0.wireOp",EDGE,"E8.0.22.8"),sQuery(id+"F0.wireOp",EDGE,"E8.0.23.0"),sQuery(id+"F0.wireOp",EDGE,"E8.0.23.1"),sQuery(id+"F0.wireOp",EDGE,"E8.0.23.2"),sQuery(id+"F0.wireOp",EDGE,"E8.0.23.3"),sQuery(id+"F0.wireOp",EDGE,"E8.0.23.4"),sQuery(id+"F0.wireOp",EDGE,"E8.0.23.5"),sQuery(id+"F0.wireOp",EDGE,"E8.0.23.6"),sQuery(id+"F0.wireOp",EDGE,"E8.0.23.7"),sQuery(id+"F0.wireOp",EDGE,"E8.0.23.8"),sQuery(id+"F0.wireOp",EDGE,"E8.0.24.0"),sQuery(id+"F0.wireOp",EDGE,"E8.0.24.1"),sQuery(id+"F0.wireOp",EDGE,"E8.0.24.2"),sQuery(id+"F0.wireOp",EDGE,"E8.0.24.3"),sQuery(id+"F0.wireOp",EDGE,"E8.0.24.4"),sQuery(id+"F0.wireOp",EDGE,"E8.0.24.5"),sQuery(id+"F0.wireOp",EDGE,"E8.0.24.6"),sQuery(id+"F0.wireOp",EDGE,"E8.0.24.7"),sQuery(id+"F0.wireOp",EDGE,"E8.0.24.8"),sQuery(id+"F0.wireOp",EDGE,"E9.0.25.0"),sQuery(id+"F0.wireOp",EDGE,"E9.0.25.1"),sQuery(id+"F0.wireOp",EDGE,"E9.0.25.2"),sQuery(id+"F0.wireOp",EDGE,"E9.0.25.3"),sQuery(id+"F0.wireOp",EDGE,"E9.0.25.4"),sQuery(id+"F0.wireOp",EDGE,"E9.0.25.5"),sQuery(id+"F0.wireOp",EDGE,"E9.0.25.6"),sQuery(id+"F0.wireOp",EDGE,"E9.0.25.7"),sQuery(id+"F0.wireOp",EDGE,"E9.0.25.8"),sQuery(id+"F0.wireOp",EDGE,"E9.0.26.0"),sQuery(id+"F0.wireOp",EDGE,"E9.0.26.1"),sQuery(id+"F0.wireOp",EDGE,"E9.0.26.2"),sQuery(id+"F0.wireOp",EDGE,"E9.0.26.3"),sQuery(id+"F0.wireOp",EDGE,"E9.0.26.4"),sQuery(id+"F0.wireOp",EDGE,"E9.0.26.5"),sQuery(id+"F0.wireOp",EDGE,"E9.0.26.6"),sQuery(id+"F0.wireOp",EDGE,"E9.0.26.7"),sQuery(id+"F0.wireOp",EDGE,"E9.0.26.8"),sQuery(id+"F0.wireOp",EDGE,"E10.0.0.9"),sQuery(id+"F0.wireOp",EDGE,"E10.0.0.10"),sQuery(id+"F0.wireOp",EDGE,"E10.0.0.11"),sQuery(id+"F0.wireOp",EDGE,"E10.0.0.12"),sQuery(id+"F0.wireOp",EDGE,"E10.0.0.13"),sQuery(id+"F0.wireOp",EDGE,"E10.0.1.9"),sQuery(id+"F0.wireOp",EDGE,"E10.0.1.10"),sQuery(id+"F0.wireOp",EDGE,"E10.0.1.11"),sQuery(id+"F0.wireOp",EDGE,"E10.0.1.12"),sQuery(id+"F0.wireOp",EDGE,"E10.0.1.13"),sQuery(id+"F0.wireOp",EDGE,"E10.0.2.9"),sQuery(id+"F0.wireOp",EDGE,"E10.0.2.10"),sQuery(id+"F0.wireOp",EDGE,"E10.0.2.11"),sQuery(id+"F0.wireOp",EDGE,"E10.0.2.12"),sQuery(id+"F0.wireOp",EDGE,"E10.0.2.13"),sQuery(id+"F0.wireOp",EDGE,"E10.0.3.9"),sQuery(id+"F0.wireOp",EDGE,"E10.0.3.10"),sQuery(id+"F0.wireOp",EDGE,"E10.0.3.11"),sQuery(id+"F0.wireOp",EDGE,"E10.0.3.12"),sQuery(id+"F0.wireOp",EDGE,"E10.0.3.13"),sQuery(id+"F0.wireOp",EDGE,"E10.0.4.9"),sQuery(id+"F0.wireOp",EDGE,"E10.0.4.10"),sQuery(id+"F0.wireOp",EDGE,"E10.0.4.11"),sQuery(id+"F0.wireOp",EDGE,"E10.0.4.12"),sQuery(id+"F0.wireOp",EDGE,"E10.0.4.13"),sQuery(id+"F0.wireOp",EDGE,"E10.0.5.9"),sQuery(id+"F0.wireOp",EDGE,"E10.0.5.10"),sQuery(id+"F0.wireOp",EDGE,"E10.0.5.11"),sQuery(id+"F0.wireOp",EDGE,"E10.0.5.12"),sQuery(id+"F0.wireOp",EDGE,"E10.0.5.13"),sQuery(id+"F0.wireOp",EDGE,"E10.0.6.9"),sQuery(id+"F0.wireOp",EDGE,"E10.0.6.10"),sQuery(id+"F0.wireOp",EDGE,"E10.0.6.11"),sQuery(id+"F0.wireOp",EDGE,"E10.0.6.12"),sQuery(id+"F0.wireOp",EDGE,"E10.0.6.13"),sQuery(id+"F0.wireOp",EDGE,"E10.0.7.9"),sQuery(id+"F0.wireOp",EDGE,"E10.0.7.10"),sQuery(id+"F0.wireOp",EDGE,"E10.0.7.11"),sQuery(id+"F0.wireOp",EDGE,"E10.0.7.12"),sQuery(id+"F0.wireOp",EDGE,"E10.0.7.13"),sQuery(id+"F0.wireOp",EDGE,"E10.0.8.9"),sQuery(id+"F0.wireOp",EDGE,"E10.0.8.10"),sQuery(id+"F0.wireOp",EDGE,"E10.0.8.11"),sQuery(id+"F0.wireOp",EDGE,"E10.0.8.12"),sQuery(id+"F0.wireOp",EDGE,"E10.0.8.13"),sQuery(id+"F0.wireOp",EDGE,"E10.0.9.9"),sQuery(id+"F0.wireOp",EDGE,"E10.0.9.10"),sQuery(id+"F0.wireOp",EDGE,"E10.0.9.11"),sQuery(id+"F0.wireOp",EDGE,"E10.0.9.12"),sQuery(id+"F0.wireOp",EDGE,"E10.0.9.13"),sQuery(id+"F0.wireOp",EDGE,"E10.0.10.9"),sQuery(id+"F0.wireOp",EDGE,"E10.0.10.10"),sQuery(id+"F0.wireOp",EDGE,"E10.0.10.11"),sQuery(id+"F0.wireOp",EDGE,"E10.0.10.12"),sQuery(id+"F0.wireOp",EDGE,"E10.0.10.13"),sQuery(id+"F0.wireOp",EDGE,"E10.0.11.9"),sQuery(id+"F0.wireOp",EDGE,"E10.0.11.10"),sQuery(id+"F0.wireOp",EDGE,"E10.0.11.11"),sQuery(id+"F0.wireOp",EDGE,"E10.0.11.12"),sQuery(id+"F0.wireOp",EDGE,"E10.0.11.13"),sQuery(id+"F0.wireOp",EDGE,"E10.0.12.9"),sQuery(id+"F0.wireOp",EDGE,"E10.0.12.10"),sQuery(id+"F0.wireOp",EDGE,"E10.0.12.11"),sQuery(id+"F0.wireOp",EDGE,"E10.0.12.12"),sQuery(id+"F0.wireOp",EDGE,"E10.0.12.13"),sQuery(id+"F0.wireOp",EDGE,"E10.0.13.9"),sQuery(id+"F0.wireOp",EDGE,"E10.0.13.10"),sQuery(id+"F0.wireOp",EDGE,"E10.0.13.11"),sQuery(id+"F0.wireOp",EDGE,"E10.0.13.12"),sQuery(id+"F0.wireOp",EDGE,"E10.0.13.13"),sQuery(id+"F0.wireOp",EDGE,"E10.0.14.9"),sQuery(id+"F0.wireOp",EDGE,"E10.0.14.10"),sQuery(id+"F0.wireOp",EDGE,"E10.0.14.11"),sQuery(id+"F0.wireOp",EDGE,"E10.0.14.12"),sQuery(id+"F0.wireOp",EDGE,"E10.0.14.13"),sQuery(id+"F0.wireOp",EDGE,"E10.0.15.9"),sQuery(id+"F0.wireOp",EDGE,"E10.0.15.10"),sQuery(id+"F0.wireOp",EDGE,"E10.0.15.11"),sQuery(id+"F0.wireOp",EDGE,"E10.0.15.12"),sQuery(id+"F0.wireOp",EDGE,"E10.0.15.13"),sQuery(id+"F0.wireOp",EDGE,"E10.0.16.9"),sQuery(id+"F0.wireOp",EDGE,"E10.0.16.10"),sQuery(id+"F0.wireOp",EDGE,"E10.0.16.11"),sQuery(id+"F0.wireOp",EDGE,"E10.0.16.12"),sQuery(id+"F0.wireOp",EDGE,"E10.0.16.13"),sQuery(id+"F0.wireOp",EDGE,"E10.0.17.9"),sQuery(id+"F0.wireOp",EDGE,"E10.0.17.10"),sQuery(id+"F0.wireOp",EDGE,"E10.0.17.11"),sQuery(id+"F0.wireOp",EDGE,"E10.0.17.12"),sQuery(id+"F0.wireOp",EDGE,"E10.0.17.13"),sQuery(id+"F0.wireOp",EDGE,"E10.0.18.9"),sQuery(id+"F0.wireOp",EDGE,"E10.0.18.10"),sQuery(id+"F0.wireOp",EDGE,"E10.0.18.11"),sQuery(id+"F0.wireOp",EDGE,"E10.0.18.12"),sQuery(id+"F0.wireOp",EDGE,"E10.0.18.13"),sQuery(id+"F0.wireOp",EDGE,"E10.0.19.9"),sQuery(id+"F0.wireOp",EDGE,"E10.0.19.10"),sQuery(id+"F0.wireOp",EDGE,"E10.0.19.11"),sQuery(id+"F0.wireOp",EDGE,"E10.0.19.12"),sQuery(id+"F0.wireOp",EDGE,"E10.0.19.13"),sQuery(id+"F0.wireOp",EDGE,"E10.0.20.9"),sQuery(id+"F0.wireOp",EDGE,"E10.0.20.10"),sQuery(id+"F0.wireOp",EDGE,"E10.0.20.11"),sQuery(id+"F0.wireOp",EDGE,"E10.0.20.12"),sQuery(id+"F0.wireOp",EDGE,"E10.0.20.13"),sQuery(id+"F0.wireOp",EDGE,"E10.0.21.9"),sQuery(id+"F0.wireOp",EDGE,"E10.0.21.10"),sQuery(id+"F0.wireOp",EDGE,"E10.0.21.11"),sQuery(id+"F0.wireOp",EDGE,"E10.0.21.12"),sQuery(id+"F0.wireOp",EDGE,"E10.0.21.13"),sQuery(id+"F0.wireOp",EDGE,"E10.0.22.9"),sQuery(id+"F0.wireOp",EDGE,"E10.0.22.10"),sQuery(id+"F0.wireOp",EDGE,"E10.0.22.11"),sQuery(id+"F0.wireOp",EDGE,"E10.0.22.12"),sQuery(id+"F0.wireOp",EDGE,"E10.0.22.13"),sQuery(id+"F0.wireOp",EDGE,"E10.0.23.9"),sQuery(id+"F0.wireOp",EDGE,"E10.0.23.10"),sQuery(id+"F0.wireOp",EDGE,"E10.0.23.11"),sQuery(id+"F0.wireOp",EDGE,"E10.0.23.12"),sQuery(id+"F0.wireOp",EDGE,"E10.0.23.13"),sQuery(id+"F0.wireOp",EDGE,"E10.0.24.9"),sQuery(id+"F0.wireOp",EDGE,"E10.0.24.10"),sQuery(id+"F0.wireOp",EDGE,"E10.0.24.11"),sQuery(id+"F0.wireOp",EDGE,"E10.0.24.12"),sQuery(id+"F0.wireOp",EDGE,"E10.0.24.13"),sQuery(id+"F0.wireOp",EDGE,"E10.0.25.9"),sQuery(id+"F0.wireOp",EDGE,"E10.0.25.10"),sQuery(id+"F0.wireOp",EDGE,"E10.0.25.11"),sQuery(id+"F0.wireOp",EDGE,"E10.0.25.12"),sQuery(id+"F0.wireOp",EDGE,"E10.0.25.13"),sQuery(id+"F0.wireOp",EDGE,"E10.0.26.9"),sQuery(id+"F0.wireOp",EDGE,"E10.0.26.10"),sQuery(id+"F0.wireOp",EDGE,"E10.0.26.11"),sQuery(id+"F0.wireOp",EDGE,"E10.0.26.12"),sQuery(id+"F0.wireOp",EDGE,"E10.0.26.13"),sQuery(id+"F0.wireOp",EDGE,"E11.0.0.14"),sQuery(id+"F0.wireOp",EDGE,"E11.0.1.14"),sQuery(id+"F0.wireOp",EDGE,"E11.0.2.14"),sQuery(id+"F0.wireOp",EDGE,"E11.0.3.14"),sQuery(id+"F0.wireOp",EDGE,"E11.0.4.14"),sQuery(id+"F0.wireOp",EDGE,"E11.0.5.14"),sQuery(id+"F0.wireOp",EDGE,"E11.0.6.14"),sQuery(id+"F0.wireOp",EDGE,"E11.0.7.14"),sQuery(id+"F0.wireOp",EDGE,"E11.0.8.14"),sQuery(id+"F0.wireOp",EDGE,"E11.0.9.14"),sQuery(id+"F0.wireOp",EDGE,"E11.0.10.14"),sQuery(id+"F0.wireOp",EDGE,"E11.0.11.14"),sQuery(id+"F0.wireOp",EDGE,"E11.0.12.14"),sQuery(id+"F0.wireOp",EDGE,"E11.0.13.14"),sQuery(id+"F0.wireOp",EDGE,"E11.0.14.14"),sQuery(id+"F0.wireOp",EDGE,"E11.0.15.14"),sQuery(id+"F0.wireOp",EDGE,"E11.0.16.14"),sQuery(id+"F0.wireOp",EDGE,"E11.0.17.14"),sQuery(id+"F0.wireOp",EDGE,"E11.0.18.14"),sQuery(id+"F0.wireOp",EDGE,"E11.0.19.14"),sQuery(id+"F0.wireOp",EDGE,"E11.0.20.14"),sQuery(id+"F0.wireOp",EDGE,"E11.0.21.14"),sQuery(id+"F0.wireOp",EDGE,"E11.0.22.14"),sQuery(id+"F0.wireOp",EDGE,"E11.0.23.14"),sQuery(id+"F0.wireOp",EDGE,"E11.0.24.14"),sQuery(id+"F0.wireOp",EDGE,"E11.0.25.14"),sQuery(id+"F0.wireOp",EDGE,"E11.0.26.14")])],"isStart":false});
            var sketch = newSketch(context, id + "F2", { "sketchPlane" : qUnion([Q0])});
            skLineSegment(sketch, "E12.0", {"start": v(-440, 275) * mm, "end": v(440, 275) * mm, "construction": true});
            skLineSegment(sketch, "E12.1", {"start": v(-440, 275) * mm, "end": v(-440, -275) * mm, "construction": true});
            skLineSegment(sketch, "E12.2", {"start": v(-440, -275) * mm, "end": v(440, -275) * mm, "construction": true});
            skLineSegment(sketch, "E12.3", {"start": v(440, 275) * mm, "end": v(440, -275) * mm, "construction": true});
            skLineSegment(sketch, "E13.0", {"start": v(-415, 250) * mm, "end": v(-415, -250) * mm, "construction": true});
            skLineSegment(sketch, "E13.1", {"start": v(-415, 250) * mm, "end": v(415, 250) * mm, "construction": true});
            skLineSegment(sketch, "E13.2", {"start": v(415, 250) * mm, "end": v(415, -250) * mm, "construction": true});
            skLineSegment(sketch, "E13.3", {"start": v(-415, -250) * mm, "end": v(415, -250) * mm, "construction": true});
            skCircle(sketch, "E14", {"center": v(-415, 250) * mm, "radius": 1.5 * mm});
            skCircle(sketch, "E15", {"center": v(415, 250) * mm, "radius": 1.5 * mm});
            skCircle(sketch, "E16", {"center": v(415, -250) * mm, "radius": 1.5 * mm});
            skCircle(sketch, "E17", {"center": v(-415, -250) * mm, "radius": 1.5 * mm});
            skSolve(sketch);
        }
        {
            var Q0;
            Q0 = qSketchRegion(id + "F2", true);
            extrude(context, id + "F3", {"entities" : qUnion([Q0]), "operationType" : NewBodyOperationType.REMOVE, "oppositeDirection" : true, "depth" : 25 * mm});
        }
        {
            var Q0;
            Q0=makeQuery(id+"F1.opExtrude","SWEPT_EDGE",EDGE,{"disambiguationData":[OSD([sQuery(id+"F0.wireOp",EDGE,"E0.bottom"),sQuery(id+"F0.wireOp",EDGE,"E0.left")])]});
            var Q1;
            Q1=makeQuery(id+"F1.opExtrude","SWEPT_EDGE",EDGE,{"disambiguationData":[OSD([sQuery(id+"F0.wireOp",EDGE,"E0.bottom"),sQuery(id+"F0.wireOp",EDGE,"E4")])]});
            var Q2;
            Q2=makeQuery(id+"F1.opExtrude","SWEPT_EDGE",EDGE,{"disambiguationData":[OSD([sQuery(id+"F0.wireOp",EDGE,"E0.top"),sQuery(id+"F0.wireOp",EDGE,"E4")])]});
            var Q3;
            Q3=makeQuery(id+"F1.opExtrude","SWEPT_EDGE",EDGE,{"disambiguationData":[OSD([sQuery(id+"F0.wireOp",EDGE,"E0.top"),sQuery(id+"F0.wireOp",EDGE,"E0.left")])]});
            fillet(context, id + "F4", {"entities" : qUnion([Q0, Q1, Q2, Q3]), "radius" : 25.4 * mm, "tangentPropagation" : true, "allowEdgeOverflow" : false});
        }
        {
            var Q0;
            Q0=makeQuery(id+"F1.opExtrude","CAP_FACE",FACE,{"disambiguationData":[OSD([sQuery(id+"F0.wireOp",EDGE,"E0.bottom"),sQuery(id+"F0.wireOp",EDGE,"E0.top"),sQuery(id+"F0.wireOp",EDGE,"E0.left"),sQuery(id+"F0.wireOp",EDGE,"E3"),sQuery(id+"F0.wireOp",EDGE,"E4"),sQuery(id+"F0.wireOp",EDGE,"E7.0.1.0"),sQuery(id+"F0.wireOp",EDGE,"E7.0.2.0"),sQuery(id+"F0.wireOp",EDGE,"E7.0.3.0"),sQuery(id+"F0.wireOp",EDGE,"E7.0.4.0"),sQuery(id+"F0.wireOp",EDGE,"E7.0.5.0"),sQuery(id+"F0.wireOp",EDGE,"E7.0.6.0"),sQuery(id+"F0.wireOp",EDGE,"E7.0.7.0"),sQuery(id+"F0.wireOp",EDGE,"E7.0.8.0"),sQuery(id+"F0.wireOp",EDGE,"E7.0.9.0"),sQuery(id+"F0.wireOp",EDGE,"E7.0.10.0"),sQuery(id+"F0.wireOp",EDGE,"E7.1.0.0"),sQuery(id+"F0.wireOp",EDGE,"E7.1.1.0"),sQuery(id+"F0.wireOp",EDGE,"E7.1.2.0"),sQuery(id+"F0.wireOp",EDGE,"E7.1.3.0"),sQuery(id+"F0.wireOp",EDGE,"E7.1.4.0"),sQuery(id+"F0.wireOp",EDGE,"E7.1.5.0"),sQuery(id+"F0.wireOp",EDGE,"E7.1.6.0"),sQuery(id+"F0.wireOp",EDGE,"E7.1.7.0"),sQuery(id+"F0.wireOp",EDGE,"E7.1.8.0"),sQuery(id+"F0.wireOp",EDGE,"E7.1.9.0"),sQuery(id+"F0.wireOp",EDGE,"E7.1.10.0"),sQuery(id+"F0.wireOp",EDGE,"E7.2.0.0"),sQuery(id+"F0.wireOp",EDGE,"E7.2.1.0"),sQuery(id+"F0.wireOp",EDGE,"E7.2.2.0"),sQuery(id+"F0.wireOp",EDGE,"E7.2.3.0"),sQuery(id+"F0.wireOp",EDGE,"E7.2.4.0"),sQuery(id+"F0.wireOp",EDGE,"E7.2.5.0"),sQuery(id+"F0.wireOp",EDGE,"E7.2.6.0"),sQuery(id+"F0.wireOp",EDGE,"E7.2.7.0"),sQuery(id+"F0.wireOp",EDGE,"E7.2.8.0"),sQuery(id+"F0.wireOp",EDGE,"E7.2.9.0"),sQuery(id+"F0.wireOp",EDGE,"E7.2.10.0"),sQuery(id+"F0.wireOp",EDGE,"E7.3.0.0"),sQuery(id+"F0.wireOp",EDGE,"E7.3.1.0"),sQuery(id+"F0.wireOp",EDGE,"E7.3.2.0"),sQuery(id+"F0.wireOp",EDGE,"E7.3.3.0"),sQuery(id+"F0.wireOp",EDGE,"E7.3.4.0"),sQuery(id+"F0.wireOp",EDGE,"E7.3.5.0"),sQuery(id+"F0.wireOp",EDGE,"E7.3.6.0"),sQuery(id+"F0.wireOp",EDGE,"E7.3.7.0"),sQuery(id+"F0.wireOp",EDGE,"E7.3.8.0"),sQuery(id+"F0.wireOp",EDGE,"E7.3.9.0"),sQuery(id+"F0.wireOp",EDGE,"E7.3.10.0"),sQuery(id+"F0.wireOp",EDGE,"E7.4.0.0"),sQuery(id+"F0.wireOp",EDGE,"E7.4.1.0"),sQuery(id+"F0.wireOp",EDGE,"E7.4.2.0"),sQuery(id+"F0.wireOp",EDGE,"E7.4.3.0"),sQuery(id+"F0.wireOp",EDGE,"E7.4.4.0"),sQuery(id+"F0.wireOp",EDGE,"E7.4.5.0"),sQuery(id+"F0.wireOp",EDGE,"E7.4.6.0"),sQuery(id+"F0.wireOp",EDGE,"E7.4.7.0"),sQuery(id+"F0.wireOp",EDGE,"E7.4.8.0"),sQuery(id+"F0.wireOp",EDGE,"E7.4.9.0"),sQuery(id+"F0.wireOp",EDGE,"E7.4.10.0"),sQuery(id+"F0.wireOp",EDGE,"E7.5.0.0"),sQuery(id+"F0.wireOp",EDGE,"E7.5.1.0"),sQuery(id+"F0.wireOp",EDGE,"E7.5.2.0"),sQuery(id+"F0.wireOp",EDGE,"E7.5.3.0"),sQuery(id+"F0.wireOp",EDGE,"E7.5.4.0"),sQuery(id+"F0.wireOp",EDGE,"E7.5.5.0"),sQuery(id+"F0.wireOp",EDGE,"E7.5.6.0"),sQuery(id+"F0.wireOp",EDGE,"E7.5.7.0"),sQuery(id+"F0.wireOp",EDGE,"E7.5.8.0"),sQuery(id+"F0.wireOp",EDGE,"E7.5.9.0"),sQuery(id+"F0.wireOp",EDGE,"E7.5.10.0"),sQuery(id+"F0.wireOp",EDGE,"E7.6.0.0"),sQuery(id+"F0.wireOp",EDGE,"E7.6.1.0"),sQuery(id+"F0.wireOp",EDGE,"E7.6.2.0"),sQuery(id+"F0.wireOp",EDGE,"E7.6.3.0"),sQuery(id+"F0.wireOp",EDGE,"E7.6.4.0"),sQuery(id+"F0.wireOp",EDGE,"E7.6.5.0"),sQuery(id+"F0.wireOp",EDGE,"E7.6.6.0"),sQuery(id+"F0.wireOp",EDGE,"E7.6.7.0"),sQuery(id+"F0.wireOp",EDGE,"E7.6.8.0"),sQuery(id+"F0.wireOp",EDGE,"E7.6.9.0"),sQuery(id+"F0.wireOp",EDGE,"E7.6.10.0"),sQuery(id+"F0.wireOp",EDGE,"E7.7.0.0"),sQuery(id+"F0.wireOp",EDGE,"E7.7.1.0"),sQuery(id+"F0.wireOp",EDGE,"E7.7.2.0"),sQuery(id+"F0.wireOp",EDGE,"E7.7.3.0"),sQuery(id+"F0.wireOp",EDGE,"E7.7.4.0"),sQuery(id+"F0.wireOp",EDGE,"E7.7.5.0"),sQuery(id+"F0.wireOp",EDGE,"E7.7.6.0"),sQuery(id+"F0.wireOp",EDGE,"E7.7.7.0"),sQuery(id+"F0.wireOp",EDGE,"E7.7.8.0"),sQuery(id+"F0.wireOp",EDGE,"E7.7.9.0"),sQuery(id+"F0.wireOp",EDGE,"E7.7.10.0"),sQuery(id+"F0.wireOp",EDGE,"E7.8.0.0"),sQuery(id+"F0.wireOp",EDGE,"E7.8.1.0"),sQuery(id+"F0.wireOp",EDGE,"E7.8.2.0"),sQuery(id+"F0.wireOp",EDGE,"E7.8.3.0"),sQuery(id+"F0.wireOp",EDGE,"E7.8.4.0"),sQuery(id+"F0.wireOp",EDGE,"E7.8.5.0"),sQuery(id+"F0.wireOp",EDGE,"E7.8.6.0"),sQuery(id+"F0.wireOp",EDGE,"E7.8.7.0"),sQuery(id+"F0.wireOp",EDGE,"E7.8.8.0"),sQuery(id+"F0.wireOp",EDGE,"E7.8.9.0"),sQuery(id+"F0.wireOp",EDGE,"E7.8.10.0"),sQuery(id+"F0.wireOp",EDGE,"E7.9.0.0"),sQuery(id+"F0.wireOp",EDGE,"E7.9.1.0"),sQuery(id+"F0.wireOp",EDGE,"E7.9.2.0"),sQuery(id+"F0.wireOp",EDGE,"E7.9.3.0"),sQuery(id+"F0.wireOp",EDGE,"E7.9.4.0"),sQuery(id+"F0.wireOp",EDGE,"E7.9.5.0"),sQuery(id+"F0.wireOp",EDGE,"E7.9.6.0"),sQuery(id+"F0.wireOp",EDGE,"E7.9.7.0"),sQuery(id+"F0.wireOp",EDGE,"E7.9.8.0"),sQuery(id+"F0.wireOp",EDGE,"E7.9.9.0"),sQuery(id+"F0.wireOp",EDGE,"E7.9.10.0"),sQuery(id+"F0.wireOp",EDGE,"E7.10.0.0"),sQuery(id+"F0.wireOp",EDGE,"E7.10.1.0"),sQuery(id+"F0.wireOp",EDGE,"E7.10.2.0"),sQuery(id+"F0.wireOp",EDGE,"E7.10.3.0"),sQuery(id+"F0.wireOp",EDGE,"E7.10.4.0"),sQuery(id+"F0.wireOp",EDGE,"E7.10.5.0"),sQuery(id+"F0.wireOp",EDGE,"E7.10.6.0"),sQuery(id+"F0.wireOp",EDGE,"E7.10.7.0"),sQuery(id+"F0.wireOp",EDGE,"E7.10.8.0"),sQuery(id+"F0.wireOp",EDGE,"E7.10.9.0"),sQuery(id+"F0.wireOp",EDGE,"E7.10.10.0"),sQuery(id+"F0.wireOp",EDGE,"E7.11.0.0"),sQuery(id+"F0.wireOp",EDGE,"E7.11.1.0"),sQuery(id+"F0.wireOp",EDGE,"E7.11.2.0"),sQuery(id+"F0.wireOp",EDGE,"E7.11.3.0"),sQuery(id+"F0.wireOp",EDGE,"E7.11.4.0"),sQuery(id+"F0.wireOp",EDGE,"E7.11.5.0"),sQuery(id+"F0.wireOp",EDGE,"E7.11.6.0"),sQuery(id+"F0.wireOp",EDGE,"E7.11.7.0"),sQuery(id+"F0.wireOp",EDGE,"E7.11.8.0"),sQuery(id+"F0.wireOp",EDGE,"E7.11.9.0"),sQuery(id+"F0.wireOp",EDGE,"E7.11.10.0"),sQuery(id+"F0.wireOp",EDGE,"E7.12.0.0"),sQuery(id+"F0.wireOp",EDGE,"E7.12.1.0"),sQuery(id+"F0.wireOp",EDGE,"E7.12.2.0"),sQuery(id+"F0.wireOp",EDGE,"E7.12.3.0"),sQuery(id+"F0.wireOp",EDGE,"E7.12.4.0"),sQuery(id+"F0.wireOp",EDGE,"E7.12.5.0"),sQuery(id+"F0.wireOp",EDGE,"E7.12.6.0"),sQuery(id+"F0.wireOp",EDGE,"E7.12.7.0"),sQuery(id+"F0.wireOp",EDGE,"E7.12.8.0"),sQuery(id+"F0.wireOp",EDGE,"E7.12.9.0"),sQuery(id+"F0.wireOp",EDGE,"E7.12.10.0"),sQuery(id+"F0.wireOp",EDGE,"E7.13.0.0"),sQuery(id+"F0.wireOp",EDGE,"E7.13.1.0"),sQuery(id+"F0.wireOp",EDGE,"E7.13.2.0"),sQuery(id+"F0.wireOp",EDGE,"E7.13.3.0"),sQuery(id+"F0.wireOp",EDGE,"E7.13.4.0"),sQuery(id+"F0.wireOp",EDGE,"E7.13.5.0"),sQuery(id+"F0.wireOp",EDGE,"E7.13.6.0"),sQuery(id+"F0.wireOp",EDGE,"E7.13.7.0"),sQuery(id+"F0.wireOp",EDGE,"E7.13.8.0"),sQuery(id+"F0.wireOp",EDGE,"E7.13.9.0"),sQuery(id+"F0.wireOp",EDGE,"E7.13.10.0"),sQuery(id+"F0.wireOp",EDGE,"E7.14.0.0"),sQuery(id+"F0.wireOp",EDGE,"E7.14.1.0"),sQuery(id+"F0.wireOp",EDGE,"E7.14.2.0"),sQuery(id+"F0.wireOp",EDGE,"E7.14.3.0"),sQuery(id+"F0.wireOp",EDGE,"E7.14.4.0"),sQuery(id+"F0.wireOp",EDGE,"E7.14.5.0"),sQuery(id+"F0.wireOp",EDGE,"E7.14.6.0"),sQuery(id+"F0.wireOp",EDGE,"E7.14.7.0"),sQuery(id+"F0.wireOp",EDGE,"E7.14.8.0"),sQuery(id+"F0.wireOp",EDGE,"E7.14.9.0"),sQuery(id+"F0.wireOp",EDGE,"E7.14.10.0"),sQuery(id+"F0.wireOp",EDGE,"E7.15.0.0"),sQuery(id+"F0.wireOp",EDGE,"E7.15.1.0"),sQuery(id+"F0.wireOp",EDGE,"E7.15.2.0"),sQuery(id+"F0.wireOp",EDGE,"E7.15.3.0"),sQuery(id+"F0.wireOp",EDGE,"E7.15.4.0"),sQuery(id+"F0.wireOp",EDGE,"E7.15.5.0"),sQuery(id+"F0.wireOp",EDGE,"E7.15.6.0"),sQuery(id+"F0.wireOp",EDGE,"E7.15.7.0"),sQuery(id+"F0.wireOp",EDGE,"E7.15.8.0"),sQuery(id+"F0.wireOp",EDGE,"E7.15.9.0"),sQuery(id+"F0.wireOp",EDGE,"E7.15.10.0"),sQuery(id+"F0.wireOp",EDGE,"E7.16.0.0"),sQuery(id+"F0.wireOp",EDGE,"E7.16.1.0"),sQuery(id+"F0.wireOp",EDGE,"E7.16.2.0"),sQuery(id+"F0.wireOp",EDGE,"E7.16.3.0"),sQuery(id+"F0.wireOp",EDGE,"E7.16.4.0"),sQuery(id+"F0.wireOp",EDGE,"E7.16.5.0"),sQuery(id+"F0.wireOp",EDGE,"E7.16.6.0"),sQuery(id+"F0.wireOp",EDGE,"E7.16.7.0"),sQuery(id+"F0.wireOp",EDGE,"E7.16.8.0"),sQuery(id+"F0.wireOp",EDGE,"E7.16.9.0"),sQuery(id+"F0.wireOp",EDGE,"E7.16.10.0")])],"isStart":false});
            var sketch = newSketch(context, id + "F5", { "sketchPlane" : qUnion([Q0])});
            skText(sketch, "E18", { "text": "Dror Galil - Maker Space", "fontName": "OpenSans-Bold.ttf"});
            const initialGuessF5  = {"E18": [-0.20831, 0.24, 1, 0, 0.025]};
            skSetInitialGuess(sketch, initialGuessF5);
            skSolve(sketch);
        }
        {
            var Q0;
            Q0 = qSketchRegion(id + "F5", true);
            extrude(context, id + "F6", {"entities" : qUnion([Q0]), "operationType" : NewBodyOperationType.REMOVE, "oppositeDirection" : true, "depth" : 2.54 * mm});
        }
    });
